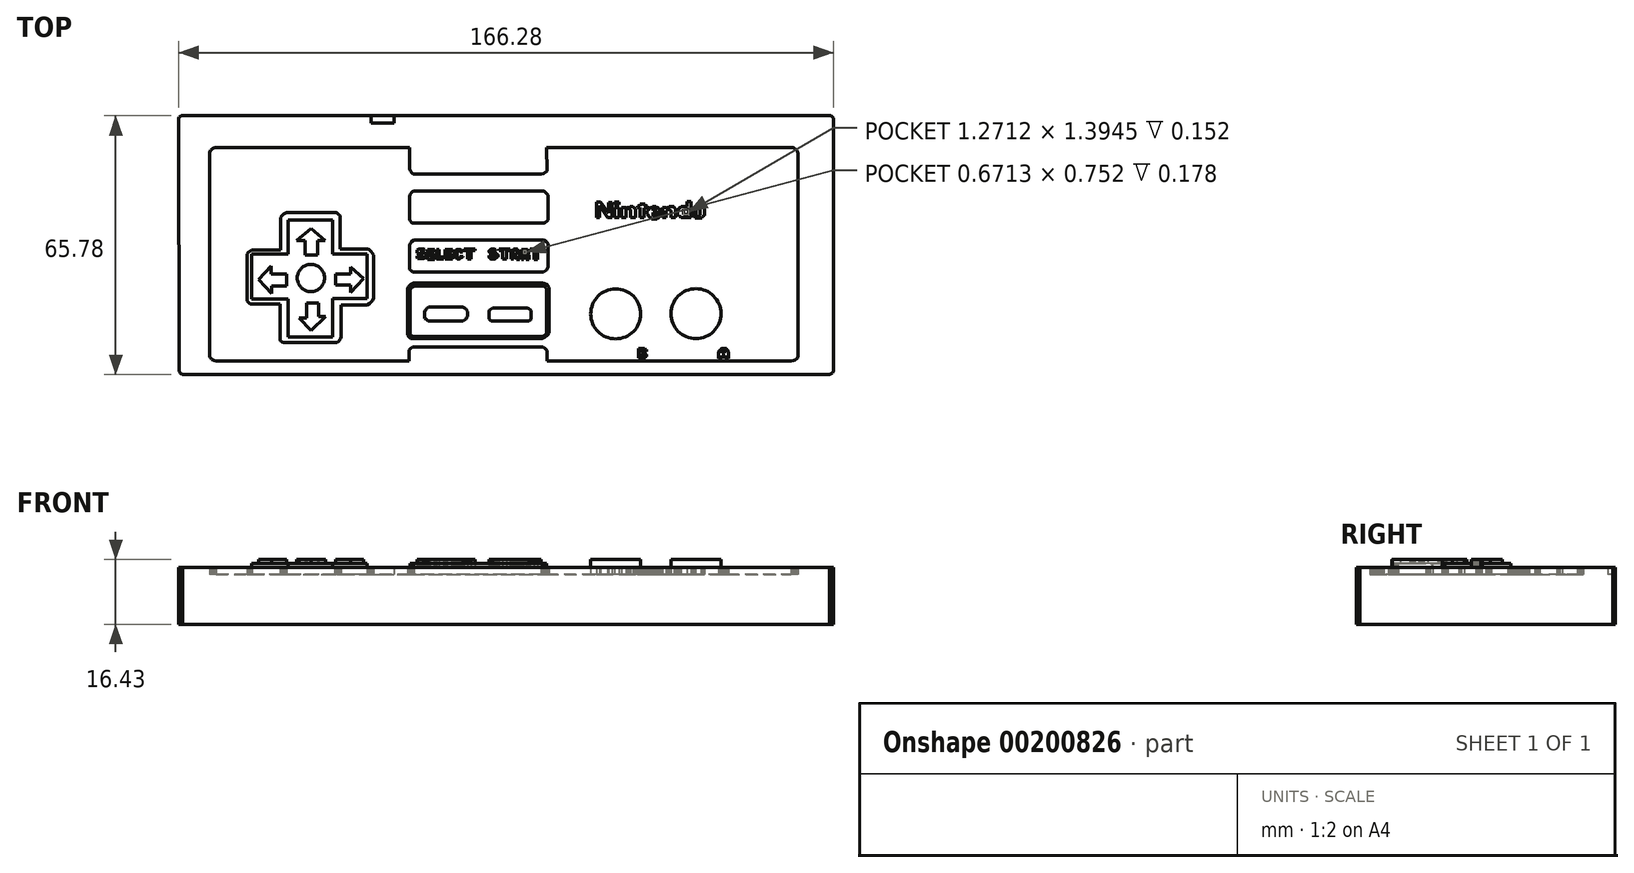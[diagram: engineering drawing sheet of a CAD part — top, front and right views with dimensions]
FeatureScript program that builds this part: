
annotation { "Feature Type Name" : "Feature", "Feature Type Description" : "" }
export const myFeature = defineFeature(function(context is Context, id is Id, definition is map)
    precondition{}
    {
        {
            var Q0;
            Q0=qCreatedBy(makeId("Top.planeOp"),FACE);
            var sketch = newSketch(context, id + "F0", { "sketchPlane" : qUnion([Q0])});
            skLineSegment(sketch, "E0", {"start": v(-67.86, 49.1) * mm, "end": v(97.18, 49.1) * mm});
            skLineSegment(sketch, "E1", {"start": v(97.81, 48.49) * mm, "end": v(97.81, -15.77) * mm});
            skLineSegment(sketch, "E2", {"start": v(96.88, -16.7) * mm, "end": v(-67.5, -16.7) * mm});
            skLineSegment(sketch, "E3", {"start": v(-68.37, -15.86) * mm, "end": v(-68.47, 48.53) * mm});
            skLineSegment(sketch, "E4", {"start": v(-59.29, 40.98) * mm, "end": v(87.55, 40.98) * mm});
            skLineSegment(sketch, "E5", {"start": v(87.1, -13.25) * mm, "end": v(-59.07, -13.25) * mm});
            skLineSegment(sketch, "E6", {"start": v(-60.62, -12.14) * mm, "end": v(-60.7, 39.73) * mm});
            skLineSegment(sketch, "E7", {"start": v(-60.7, 39.73) * mm, "end": v(-60.56, 40.11) * mm});
            skLineSegment(sketch, "E8", {"start": v(-60.56, 40.11) * mm, "end": v(-60.37, 40.33) * mm});
            skLineSegment(sketch, "E9", {"start": v(-60.37, 40.33) * mm, "end": v(-60.1, 40.54) * mm});
            skLineSegment(sketch, "E10", {"start": v(-60.1, 40.54) * mm, "end": v(-59.86, 40.75) * mm});
            skLineSegment(sketch, "E11", {"start": v(-59.86, 40.75) * mm, "end": v(-59.62, 40.87) * mm});
            skLineSegment(sketch, "E12", {"start": v(-59.62, 40.87) * mm, "end": v(-59.29, 40.98) * mm});
            skLineSegment(sketch, "E13", {"start": v(-68.47, 48.53) * mm, "end": v(-68.36, 48.7) * mm});
            skLineSegment(sketch, "E14", {"start": v(-68.36, 48.7) * mm, "end": v(-68.18, 48.87) * mm});
            skLineSegment(sketch, "E15", {"start": v(-68.18, 48.87) * mm, "end": v(-68.01, 48.99) * mm});
            skLineSegment(sketch, "E16", {"start": v(-68.01, 48.99) * mm, "end": v(-67.86, 49.1) * mm});
            skLineSegment(sketch, "E17", {"start": v(-68.37, -15.86) * mm, "end": v(-68.29, -16.07) * mm});
            skLineSegment(sketch, "E18", {"start": v(-68.29, -16.07) * mm, "end": v(-68.14, -16.24) * mm});
            skLineSegment(sketch, "E19", {"start": v(-68.14, -16.24) * mm, "end": v(-67.97, -16.42) * mm});
            skLineSegment(sketch, "E20", {"start": v(-67.97, -16.42) * mm, "end": v(-67.8, -16.53) * mm});
            skLineSegment(sketch, "E21", {"start": v(-67.8, -16.53) * mm, "end": v(-67.64, -16.64) * mm});
            skLineSegment(sketch, "E22", {"start": v(-67.64, -16.64) * mm, "end": v(-67.5, -16.7) * mm});
            skLineSegment(sketch, "E23", {"start": v(96.88, -16.7) * mm, "end": v(97.12, -16.6) * mm});
            skLineSegment(sketch, "E24", {"start": v(97.12, -16.6) * mm, "end": v(97.35, -16.42) * mm});
            skLineSegment(sketch, "E25", {"start": v(97.35, -16.42) * mm, "end": v(97.58, -16.25) * mm});
            skLineSegment(sketch, "E26", {"start": v(97.58, -16.25) * mm, "end": v(97.75, -16.1) * mm});
            skLineSegment(sketch, "E27", {"start": v(97.75, -16.1) * mm, "end": v(97.81, -15.77) * mm});
            skLineSegment(sketch, "E28", {"start": v(97.81, 48.49) * mm, "end": v(97.7, 48.62) * mm});
            skLineSegment(sketch, "E29", {"start": v(97.7, 48.62) * mm, "end": v(97.62, 48.75) * mm});
            skLineSegment(sketch, "E30", {"start": v(97.62, 48.75) * mm, "end": v(97.48, 48.9) * mm});
            skLineSegment(sketch, "E31", {"start": v(97.48, 48.9) * mm, "end": v(97.4, 49) * mm});
            skLineSegment(sketch, "E32", {"start": v(97.4, 49) * mm, "end": v(97.18, 49.1) * mm});
            skLineSegment(sketch, "E33", {"start": v(87.55, 40.98) * mm, "end": v(87.83, 40.9) * mm});
            skLineSegment(sketch, "E34", {"start": v(87.83, 40.9) * mm, "end": v(88.15, 40.66) * mm});
            skLineSegment(sketch, "E35", {"start": v(88.15, 40.66) * mm, "end": v(88.37, 40.45) * mm});
            skLineSegment(sketch, "E36", {"start": v(88.37, 40.45) * mm, "end": v(88.55, 40.26) * mm});
            skLineSegment(sketch, "E37", {"start": v(88.55, 40.26) * mm, "end": v(88.7, 39.95) * mm});
            skLineSegment(sketch, "E38", {"start": v(88.7, 39.95) * mm, "end": v(88.83, 39.45) * mm});
            skLineSegment(sketch, "E39", {"start": v(-60.62, -12.14) * mm, "end": v(-60.52, -12.37) * mm});
            skLineSegment(sketch, "E40", {"start": v(-60.52, -12.37) * mm, "end": v(-60.33, -12.6) * mm});
            skLineSegment(sketch, "E41", {"start": v(-60.33, -12.6) * mm, "end": v(-60.1, -12.81) * mm});
            skLineSegment(sketch, "E42", {"start": v(-60.1, -12.81) * mm, "end": v(-59.8, -12.99) * mm});
            skLineSegment(sketch, "E43", {"start": v(-59.8, -12.99) * mm, "end": v(-59.51, -13.14) * mm});
            skLineSegment(sketch, "E44", {"start": v(-59.51, -13.14) * mm, "end": v(-59.07, -13.25) * mm});
            skLineSegment(sketch, "E45", {"start": v(87.1, -13.25) * mm, "end": v(87.72, -13.15) * mm});
            skLineSegment(sketch, "E46", {"start": v(87.72, -13.15) * mm, "end": v(88.1, -12.98) * mm});
            skLineSegment(sketch, "E47", {"start": v(88.1, -12.98) * mm, "end": v(88.5, -12.67) * mm});
            skLineSegment(sketch, "E48", {"start": v(88.5, -12.67) * mm, "end": v(88.67, -12.46) * mm});
            skLineSegment(sketch, "E49", {"start": v(88.67, -12.46) * mm, "end": v(88.83, -11.98) * mm});
            skCircle(sketch, "E50", {"center": v(42.5, -1.27) * mm, "radius": 6.35 * mm});
            skCircle(sketch, "E51", {"center": v(62.9, -1.22) * mm, "radius": 6.35 * mm});
            skLineSegment(sketch, "E52", {"start": v(48.28, -10.13) * mm, "end": v(48.28, -12.48) * mm});
            skLineSegment(sketch, "E53", {"start": v(48.28, -12.48) * mm, "end": v(49.67, -12.48) * mm});
            skLineSegment(sketch, "E54", {"start": v(49.87, -12.33) * mm, "end": v(50.1, -12.33) * mm});
            skLineSegment(sketch, "E55", {"start": v(50.1, -12.33) * mm, "end": v(50.1, -12.13) * mm});
            skLineSegment(sketch, "E56", {"start": v(50.1, -12.13) * mm, "end": v(50.3, -12.13) * mm});
            skLineSegment(sketch, "E57", {"start": v(50.3, -12.13) * mm, "end": v(50.3, -11.55) * mm});
            skLineSegment(sketch, "E58", {"start": v(50.3, -11.55) * mm, "end": v(50.14, -11.55) * mm});
            skLineSegment(sketch, "E59", {"start": v(50.14, -11.55) * mm, "end": v(50.14, -11.38) * mm});
            skLineSegment(sketch, "E60", {"start": v(50.14, -11.38) * mm, "end": v(49.9, -11.38) * mm});
            skLineSegment(sketch, "E61", {"start": v(49.9, -11.38) * mm, "end": v(49.9, -11.26) * mm});
            skLineSegment(sketch, "E62", {"start": v(49.9, -11.26) * mm, "end": v(49.67, -11.26) * mm});
            skLineSegment(sketch, "E63", {"start": v(49.67, -11.26) * mm, "end": v(49.67, -11.02) * mm});
            skLineSegment(sketch, "E64", {"start": v(49.67, -11.02) * mm, "end": v(49.85, -11.02) * mm});
            skLineSegment(sketch, "E65", {"start": v(49.85, -11.02) * mm, "end": v(49.85, -10.82) * mm});
            skLineSegment(sketch, "E66", {"start": v(49.85, -10.82) * mm, "end": v(50.29, -10.82) * mm});
            skLineSegment(sketch, "E67", {"start": v(50.29, -10.82) * mm, "end": v(50.29, -10.28) * mm});
            skLineSegment(sketch, "E68", {"start": v(50.29, -10.28) * mm, "end": v(49.87, -10.28) * mm});
            skLineSegment(sketch, "E69", {"start": v(49.87, -10.28) * mm, "end": v(49.87, -10.05) * mm});
            skLineSegment(sketch, "E70", {"start": v(49.87, -10.05) * mm, "end": v(48.28, -10.05) * mm});
            skLineSegment(sketch, "E71", {"start": v(48.28, -10.05) * mm, "end": v(48.28, -10.13) * mm});
            skLineSegment(sketch, "E72", {"start": v(49.67, -12.48) * mm, "end": v(49.67, -12.33) * mm});
            skLineSegment(sketch, "E73", {"start": v(49.67, -12.33) * mm, "end": v(49.87, -12.33) * mm});
            skLineSegment(sketch, "E74", {"start": v(49.01, -10.2) * mm, "end": v(49.38, -10.2) * mm});
            skLineSegment(sketch, "E75", {"start": v(49.38, -10.2) * mm, "end": v(49.51, -10.33) * mm});
            skLineSegment(sketch, "E76", {"start": v(48.9, -10.3) * mm, "end": v(49.01, -10.2) * mm});
            skLineSegment(sketch, "E77", {"start": v(49.51, -10.33) * mm, "end": v(49.51, -10.82) * mm});
            skLineSegment(sketch, "E78", {"start": v(49.51, -10.82) * mm, "end": v(49.4, -10.98) * mm});
            skLineSegment(sketch, "E79", {"start": v(49.4, -10.98) * mm, "end": v(49.02, -10.98) * mm});
            skLineSegment(sketch, "E80", {"start": v(49.02, -10.98) * mm, "end": v(48.9, -10.82) * mm});
            skLineSegment(sketch, "E81", {"start": v(48.9, -10.82) * mm, "end": v(48.9, -10.3) * mm});
            skLineSegment(sketch, "E82", {"start": v(49.02, -11.4) * mm, "end": v(49.33, -11.4) * mm});
            skLineSegment(sketch, "E83", {"start": v(49.33, -11.4) * mm, "end": v(49.45, -11.55) * mm});
            skLineSegment(sketch, "E84", {"start": v(49.45, -11.55) * mm, "end": v(49.45, -12.1) * mm});
            skLineSegment(sketch, "E85", {"start": v(49.45, -12.1) * mm, "end": v(49.33, -12.2) * mm});
            skLineSegment(sketch, "E86", {"start": v(49.33, -12.2) * mm, "end": v(49.01, -12.2) * mm});
            skLineSegment(sketch, "E87", {"start": v(49.01, -12.2) * mm, "end": v(48.91, -12.1) * mm});
            skLineSegment(sketch, "E88", {"start": v(48.91, -12.1) * mm, "end": v(48.91, -11.55) * mm});
            skLineSegment(sketch, "E89", {"start": v(48.91, -11.55) * mm, "end": v(49.02, -11.4) * mm});
            skLineSegment(sketch, "E90", {"start": v(68.62, -12.62) * mm, "end": v(69.49, -12.62) * mm});
            skLineSegment(sketch, "E91", {"start": v(69.49, -12.62) * mm, "end": v(69.49, -11.82) * mm});
            skLineSegment(sketch, "E92", {"start": v(69.49, -11.82) * mm, "end": v(70.26, -11.82) * mm});
            skLineSegment(sketch, "E93", {"start": v(70.26, -11.82) * mm, "end": v(70.26, -12.62) * mm});
            skLineSegment(sketch, "E94", {"start": v(70.26, -12.62) * mm, "end": v(71.22, -12.62) * mm});
            skLineSegment(sketch, "E95", {"start": v(71.22, -12.62) * mm, "end": v(71.22, -10.98) * mm});
            skLineSegment(sketch, "E96", {"start": v(71.22, -10.98) * mm, "end": v(71.09, -10.98) * mm});
            skLineSegment(sketch, "E97", {"start": v(71.09, -10.98) * mm, "end": v(71.09, -10.61) * mm});
            skLineSegment(sketch, "E98", {"start": v(71.09, -10.61) * mm, "end": v(70.87, -10.61) * mm});
            skLineSegment(sketch, "E99", {"start": v(70.87, -10.61) * mm, "end": v(70.87, -10.27) * mm});
            skLineSegment(sketch, "E100", {"start": v(70.87, -10.27) * mm, "end": v(70.7, -10.27) * mm});
            skLineSegment(sketch, "E101", {"start": v(70.7, -10.27) * mm, "end": v(70.7, -10.06) * mm});
            skLineSegment(sketch, "E102", {"start": v(70.7, -10.06) * mm, "end": v(69.34, -10.06) * mm});
            skLineSegment(sketch, "E103", {"start": v(69.34, -10.06) * mm, "end": v(69.34, -10.16) * mm});
            skLineSegment(sketch, "E104", {"start": v(69.34, -10.16) * mm, "end": v(69.15, -10.16) * mm});
            skLineSegment(sketch, "E105", {"start": v(69.15, -10.16) * mm, "end": v(69.15, -10.3) * mm});
            skLineSegment(sketch, "E106", {"start": v(69.15, -10.3) * mm, "end": v(68.98, -10.3) * mm});
            skLineSegment(sketch, "E107", {"start": v(68.98, -10.3) * mm, "end": v(68.98, -10.53) * mm});
            skLineSegment(sketch, "E108", {"start": v(68.98, -10.53) * mm, "end": v(68.76, -10.53) * mm});
            skLineSegment(sketch, "E109", {"start": v(68.76, -10.53) * mm, "end": v(68.76, -10.98) * mm});
            skPoint(sketch, "E109.endSnap0", {"position": v(71.15, -10.98) * mm});
            skLineSegment(sketch, "E110", {"start": v(68.76, -10.98) * mm, "end": v(68.62, -10.98) * mm});
            skLineSegment(sketch, "E111", {"start": v(68.62, -10.98) * mm, "end": v(68.62, -12.62) * mm});
            skLineSegment(sketch, "E112", {"start": v(69.54, -11.2) * mm, "end": v(70.2, -11.2) * mm});
            skLineSegment(sketch, "E113", {"start": v(70.2, -11.2) * mm, "end": v(70.2, -10.57) * mm});
            skLineSegment(sketch, "E114", {"start": v(70.2, -10.57) * mm, "end": v(70.05, -10.57) * mm});
            skLineSegment(sketch, "E115", {"start": v(70.05, -10.57) * mm, "end": v(70.05, -10.32) * mm});
            skLineSegment(sketch, "E116", {"start": v(70.05, -10.32) * mm, "end": v(69.76, -10.32) * mm});
            skLineSegment(sketch, "E117", {"start": v(69.76, -10.32) * mm, "end": v(69.76, -10.57) * mm});
            skLineSegment(sketch, "E118", {"start": v(69.76, -10.57) * mm, "end": v(69.54, -10.57) * mm});
            skLineSegment(sketch, "E119", {"start": v(69.54, -10.57) * mm, "end": v(69.54, -11.2) * mm});
            skCircle(sketch, "E120", {"center": v(-34.93, 7.86) * mm, "radius": 3.45 * mm});
            skLineSegment(sketch, "E121", {"start": v(-6, 14.79) * mm, "end": v(-6, 15.14) * mm});
            skLineSegment(sketch, "E122", {"start": v(-6, 15.14) * mm, "end": v(-6.3, 15.25) * mm});
            skLineSegment(sketch, "E123", {"start": v(-6.3, 15.25) * mm, "end": v(-6.6, 15.25) * mm});
            skLineSegment(sketch, "E124", {"start": v(-6.6, 15.25) * mm, "end": v(-7.12, 15.25) * mm});
            skLineSegment(sketch, "E125", {"start": v(-7.12, 15.25) * mm, "end": v(-7.4, 15.25) * mm});
            skLineSegment(sketch, "E126", {"start": v(-7.4, 15.25) * mm, "end": v(-7.74, 15.12) * mm});
            skLineSegment(sketch, "E127", {"start": v(-7.74, 15.12) * mm, "end": v(-7.9, 14.94) * mm});
            skLineSegment(sketch, "E128", {"start": v(-7.9, 14.94) * mm, "end": v(-7.9, 14.53) * mm});
            skLineSegment(sketch, "E129", {"start": v(-7.9, 14.53) * mm, "end": v(-7.9, 14.2) * mm});
            skLineSegment(sketch, "E130", {"start": v(-7.9, 14.2) * mm, "end": v(-7.72, 14.03) * mm});
            skLineSegment(sketch, "E131", {"start": v(-7.72, 14.03) * mm, "end": v(-7.44, 13.9) * mm});
            skLineSegment(sketch, "E132", {"start": v(-7.44, 13.9) * mm, "end": v(-7.07, 13.9) * mm});
            skLineSegment(sketch, "E133", {"start": v(-7.07, 13.9) * mm, "end": v(-6.62, 13.75) * mm});
            skLineSegment(sketch, "E134", {"start": v(-6.62, 13.75) * mm, "end": v(-6.45, 13.57) * mm});
            skLineSegment(sketch, "E135", {"start": v(-6.45, 13.57) * mm, "end": v(-6.45, 13.37) * mm});
            skLineSegment(sketch, "E136", {"start": v(-6.45, 13.37) * mm, "end": v(-6.6, 13.27) * mm});
            skLineSegment(sketch, "E137", {"start": v(-6.6, 13.27) * mm, "end": v(-7.28, 13.27) * mm});
            skLineSegment(sketch, "E138", {"start": v(-7.28, 13.27) * mm, "end": v(-7.55, 13.44) * mm});
            skLineSegment(sketch, "E139", {"start": v(-7.55, 13.44) * mm, "end": v(-7.9, 13.44) * mm});
            skLineSegment(sketch, "E140", {"start": v(-7.9, 13.44) * mm, "end": v(-7.9, 13.15) * mm});
            skLineSegment(sketch, "E141", {"start": v(-7.9, 13.15) * mm, "end": v(-7.76, 12.81) * mm});
            skLineSegment(sketch, "E142", {"start": v(-7.76, 12.81) * mm, "end": v(-7.37, 12.81) * mm});
            skLineSegment(sketch, "E143", {"start": v(-7.37, 12.81) * mm, "end": v(-6.74, 12.81) * mm});
            skLineSegment(sketch, "E144", {"start": v(-6.74, 12.81) * mm, "end": v(-6.24, 12.81) * mm});
            skLineSegment(sketch, "E145", {"start": v(-6.24, 12.81) * mm, "end": v(-5.81, 13.02) * mm});
            skLineSegment(sketch, "E146", {"start": v(-5.81, 13.02) * mm, "end": v(-5.67, 13.3) * mm});
            skLineSegment(sketch, "E147", {"start": v(-5.67, 13.3) * mm, "end": v(-5.57, 13.57) * mm});
            skLineSegment(sketch, "E148", {"start": v(-5.57, 13.57) * mm, "end": v(-5.68, 13.84) * mm});
            skLineSegment(sketch, "E149", {"start": v(-5.68, 13.84) * mm, "end": v(-5.93, 14.06) * mm});
            skLineSegment(sketch, "E150", {"start": v(-5.93, 14.06) * mm, "end": v(-6.23, 14.24) * mm});
            skLineSegment(sketch, "E151", {"start": v(-6.23, 14.24) * mm, "end": v(-6.76, 14.24) * mm});
            skLineSegment(sketch, "E152", {"start": v(-6.76, 14.24) * mm, "end": v(-7.05, 14.37) * mm});
            skLineSegment(sketch, "E153", {"start": v(-7.05, 14.37) * mm, "end": v(-7.16, 14.55) * mm});
            skLineSegment(sketch, "E154", {"start": v(-7.16, 14.55) * mm, "end": v(-6.99, 14.67) * mm});
            skLineSegment(sketch, "E155", {"start": v(-6.99, 14.67) * mm, "end": v(-6.7, 14.67) * mm});
            skLineSegment(sketch, "E156", {"start": v(-6.7, 14.67) * mm, "end": v(-6.24, 14.67) * mm});
            skLineSegment(sketch, "E157", {"start": v(-6.24, 14.67) * mm, "end": v(-6, 14.79) * mm});
            skLineSegment(sketch, "E158", {"start": v(-3.45, 15.14) * mm, "end": v(-3.45, 14.79) * mm});
            skLineSegment(sketch, "E159", {"start": v(-3.45, 14.79) * mm, "end": v(-4.75, 14.79) * mm});
            skLineSegment(sketch, "E160", {"start": v(-4.75, 14.79) * mm, "end": v(-4.75, 14.07) * mm});
            skLineSegment(sketch, "E161", {"start": v(-4.75, 14.07) * mm, "end": v(-3.68, 14.07) * mm});
            skLineSegment(sketch, "E162", {"start": v(-3.68, 14.07) * mm, "end": v(-3.68, 13.7) * mm});
            skLineSegment(sketch, "E163", {"start": v(-3.68, 13.7) * mm, "end": v(-4.68, 13.7) * mm});
            skLineSegment(sketch, "E164", {"start": v(-4.68, 13.7) * mm, "end": v(-4.68, 13.12) * mm});
            skLineSegment(sketch, "E165", {"start": v(-4.68, 13.12) * mm, "end": v(-3.48, 13.12) * mm});
            skLineSegment(sketch, "E166", {"start": v(-3.48, 13.12) * mm, "end": v(-3.48, 12.6) * mm});
            skLineSegment(sketch, "E167", {"start": v(-3.48, 12.6) * mm, "end": v(-5.3, 12.6) * mm});
            skLineSegment(sketch, "E168", {"start": v(-5.3, 12.6) * mm, "end": v(-5.3, 15.14) * mm});
            skPoint(sketch, "E169.start.orphan", {"position": v(-5.3, 15.14) * mm});
            skLineSegment(sketch, "E170", {"start": v(-3.45, 15.14) * mm, "end": v(-5.3, 15.14) * mm});
            skLineSegment(sketch, "E171", {"start": v(-2.89, 15.14) * mm, "end": v(-2.33, 15.14) * mm});
            skLineSegment(sketch, "E172", {"start": v(-2.33, 15.14) * mm, "end": v(-2.33, 13.12) * mm});
            skLineSegment(sketch, "E173", {"start": v(-2.33, 13.12) * mm, "end": v(-1.24, 13.12) * mm});
            skLineSegment(sketch, "E174", {"start": v(-1.24, 13.12) * mm, "end": v(-1.24, 12.61) * mm});
            skLineSegment(sketch, "E175", {"start": v(-1.24, 12.61) * mm, "end": v(-2.94, 12.61) * mm});
            skLineSegment(sketch, "E176", {"start": v(-2.94, 12.61) * mm, "end": v(-2.94, 15.14) * mm});
            skLineSegment(sketch, "E177", {"start": v(-0.76, 15.14) * mm, "end": v(1.05, 15.14) * mm});
            skLineSegment(sketch, "E178", {"start": v(1.05, 15.14) * mm, "end": v(1.05, 14.76) * mm});
            skLineSegment(sketch, "E179", {"start": v(1.05, 14.76) * mm, "end": v(-0.32, 14.76) * mm});
            skLineSegment(sketch, "E180", {"start": v(-0.32, 14.76) * mm, "end": v(-0.32, 14.07) * mm});
            skLineSegment(sketch, "E181", {"start": v(-0.32, 14.07) * mm, "end": v(0.87, 14.07) * mm});
            skLineSegment(sketch, "E182", {"start": v(0.87, 14.07) * mm, "end": v(0.87, 13.65) * mm});
            skLineSegment(sketch, "E183", {"start": v(0.87, 13.65) * mm, "end": v(-0.32, 13.65) * mm});
            skLineSegment(sketch, "E184", {"start": v(-0.32, 13.65) * mm, "end": v(-0.32, 13.14) * mm});
            skLineSegment(sketch, "E185", {"start": v(-0.32, 13.14) * mm, "end": v(1.09, 13.14) * mm});
            skLineSegment(sketch, "E186", {"start": v(1.09, 13.14) * mm, "end": v(1.09, 12.62) * mm});
            skLineSegment(sketch, "E187", {"start": v(1.09, 12.62) * mm, "end": v(-0.85, 12.62) * mm});
            skLineSegment(sketch, "E188", {"start": v(-0.85, 12.62) * mm, "end": v(-0.85, 15.14) * mm});
            skLineSegment(sketch, "E189", {"start": v(-0.85, 15.14) * mm, "end": v(-0.76, 15.14) * mm});
            skLineSegment(sketch, "E190", {"start": v(2.97, 14.4) * mm, "end": v(3.62, 14.4) * mm});
            skLineSegment(sketch, "E191", {"start": v(3.62, 14.4) * mm, "end": v(3.62, 14.53) * mm});
            skLineSegment(sketch, "E192", {"start": v(3.62, 14.53) * mm, "end": v(3.47, 14.53) * mm});
            skLineSegment(sketch, "E193", {"start": v(3.47, 14.53) * mm, "end": v(3.47, 14.66) * mm});
            skLineSegment(sketch, "E194", {"start": v(3.47, 14.66) * mm, "end": v(3.38, 14.66) * mm});
            skLineSegment(sketch, "E195", {"start": v(3.38, 14.66) * mm, "end": v(3.38, 14.9) * mm});
            skLineSegment(sketch, "E196", {"start": v(3.38, 14.9) * mm, "end": v(3.07, 14.9) * mm});
            skLineSegment(sketch, "E197", {"start": v(3.07, 14.9) * mm, "end": v(3.07, 15.14) * mm});
            skLineSegment(sketch, "E198", {"start": v(3.07, 15.14) * mm, "end": v(2.13, 15.14) * mm});
            skLineSegment(sketch, "E199", {"start": v(2.13, 15.14) * mm, "end": v(2.13, 14.9) * mm});
            skLineSegment(sketch, "E200", {"start": v(2.13, 14.9) * mm, "end": v(1.84, 14.9) * mm});
            skLineSegment(sketch, "E201", {"start": v(1.84, 14.9) * mm, "end": v(1.84, 14.7) * mm});
            skLineSegment(sketch, "E202", {"start": v(1.84, 14.7) * mm, "end": v(1.62, 14.7) * mm});
            skLineSegment(sketch, "E203", {"start": v(1.62, 14.7) * mm, "end": v(1.62, 13.18) * mm});
            skLineSegment(sketch, "E204", {"start": v(1.62, 13.18) * mm, "end": v(1.84, 13.18) * mm});
            skLineSegment(sketch, "E205", {"start": v(1.84, 13.18) * mm, "end": v(1.84, 12.86) * mm});
            skLineSegment(sketch, "E206", {"start": v(1.84, 12.86) * mm, "end": v(2.16, 12.86) * mm});
            skLineSegment(sketch, "E207", {"start": v(2.16, 12.86) * mm, "end": v(2.16, 12.64) * mm});
            skLineSegment(sketch, "E208", {"start": v(2.16, 12.64) * mm, "end": v(2.83, 12.64) * mm});
            skLineSegment(sketch, "E209", {"start": v(2.83, 12.64) * mm, "end": v(2.83, 12.85) * mm});
            skLineSegment(sketch, "E210", {"start": v(2.83, 12.85) * mm, "end": v(3.07, 12.85) * mm});
            skLineSegment(sketch, "E211", {"start": v(3.07, 12.85) * mm, "end": v(3.07, 13.02) * mm});
            skLineSegment(sketch, "E212", {"start": v(3.07, 13.02) * mm, "end": v(3.46, 13.02) * mm});
            skLineSegment(sketch, "E213", {"start": v(3.46, 13.02) * mm, "end": v(3.46, 13.23) * mm});
            skLineSegment(sketch, "E214", {"start": v(3.46, 13.23) * mm, "end": v(3.67, 13.23) * mm});
            skLineSegment(sketch, "E215", {"start": v(3.67, 13.23) * mm, "end": v(3.67, 13.36) * mm});
            skLineSegment(sketch, "E216", {"start": v(3.67, 13.36) * mm, "end": v(2.97, 13.36) * mm});
            skLineSegment(sketch, "E217", {"start": v(2.97, 13.36) * mm, "end": v(2.97, 13.15) * mm});
            skLineSegment(sketch, "E218", {"start": v(2.97, 13.15) * mm, "end": v(2.88, 13.15) * mm});
            skLineSegment(sketch, "E219", {"start": v(2.88, 13.15) * mm, "end": v(2.88, 12.96) * mm});
            skLineSegment(sketch, "E220", {"start": v(2.88, 12.96) * mm, "end": v(2.43, 12.96) * mm});
            skLineSegment(sketch, "E221", {"start": v(2.43, 12.96) * mm, "end": v(2.33, 12.96) * mm});
            skLineSegment(sketch, "E222", {"start": v(2.33, 12.96) * mm, "end": v(2.33, 13.06) * mm});
            skLineSegment(sketch, "E223", {"start": v(2.33, 13.06) * mm, "end": v(2.2, 13.06) * mm});
            skLineSegment(sketch, "E224", {"start": v(2.2, 13.06) * mm, "end": v(2.2, 14.67) * mm});
            skLineSegment(sketch, "E225", {"start": v(2.2, 14.67) * mm, "end": v(2.38, 14.67) * mm});
            skLineSegment(sketch, "E226", {"start": v(2.38, 14.67) * mm, "end": v(2.38, 14.92) * mm});
            skLineSegment(sketch, "E227", {"start": v(2.38, 14.92) * mm, "end": v(2.72, 14.92) * mm});
            skLineSegment(sketch, "E228", {"start": v(2.72, 14.92) * mm, "end": v(2.72, 14.69) * mm});
            skLineSegment(sketch, "E229", {"start": v(2.72, 14.69) * mm, "end": v(2.97, 14.69) * mm});
            skLineSegment(sketch, "E230", {"start": v(2.97, 14.69) * mm, "end": v(2.97, 14.4) * mm});
            skLineSegment(sketch, "E231", {"start": v(4.91, 12.64) * mm, "end": v(5.72, 12.64) * mm});
            skLineSegment(sketch, "E232", {"start": v(5.72, 12.64) * mm, "end": v(5.72, 14.87) * mm});
            skLineSegment(sketch, "E233", {"start": v(5.72, 14.87) * mm, "end": v(6.8, 14.87) * mm});
            skLineSegment(sketch, "E234", {"start": v(6.8, 14.87) * mm, "end": v(6.8, 15.23) * mm});
            skLineSegment(sketch, "E235", {"start": v(6.8, 15.23) * mm, "end": v(3.93, 15.23) * mm});
            skLineSegment(sketch, "E236", {"start": v(3.93, 15.23) * mm, "end": v(3.93, 14.87) * mm});
            skLineSegment(sketch, "E237", {"start": v(3.93, 14.87) * mm, "end": v(4.91, 14.87) * mm});
            skLineSegment(sketch, "E238", {"start": v(4.91, 14.87) * mm, "end": v(4.91, 12.64) * mm});
            skLineSegment(sketch, "E239", {"start": v(12.17, 14.77) * mm, "end": v(12.17, 15.1) * mm});
            skLineSegment(sketch, "E240", {"start": v(12.17, 15.1) * mm, "end": v(11.77, 15.1) * mm});
            skLineSegment(sketch, "E241", {"start": v(11.77, 15.1) * mm, "end": v(11.77, 15.25) * mm});
            skLineSegment(sketch, "E242", {"start": v(11.77, 15.25) * mm, "end": v(10.88, 15.25) * mm});
            skLineSegment(sketch, "E243", {"start": v(10.88, 15.25) * mm, "end": v(10.88, 15.12) * mm});
            skLineSegment(sketch, "E244", {"start": v(10.88, 15.12) * mm, "end": v(10.54, 15.12) * mm});
            skLineSegment(sketch, "E245", {"start": v(10.54, 15.12) * mm, "end": v(10.54, 14.99) * mm});
            skLineSegment(sketch, "E246", {"start": v(10.54, 14.99) * mm, "end": v(10.44, 14.99) * mm});
            skLineSegment(sketch, "E247", {"start": v(10.44, 14.99) * mm, "end": v(10.44, 14.87) * mm});
            skLineSegment(sketch, "E248", {"start": v(10.44, 14.87) * mm, "end": v(10.31, 14.87) * mm});
            skLineSegment(sketch, "E249", {"start": v(10.31, 14.87) * mm, "end": v(10.31, 14.4) * mm});
            skLineSegment(sketch, "E250", {"start": v(10.31, 14.4) * mm, "end": v(10.42, 14.4) * mm});
            skLineSegment(sketch, "E251", {"start": v(10.42, 14.4) * mm, "end": v(10.42, 14.21) * mm});
            skLineSegment(sketch, "E252", {"start": v(10.42, 14.21) * mm, "end": v(10.7, 14.21) * mm});
            skLineSegment(sketch, "E253", {"start": v(10.7, 14.21) * mm, "end": v(10.7, 13.94) * mm});
            skLineSegment(sketch, "E254", {"start": v(10.7, 13.94) * mm, "end": v(11.36, 13.94) * mm});
            skLineSegment(sketch, "E255", {"start": v(11.36, 13.94) * mm, "end": v(11.36, 13.7) * mm});
            skLineSegment(sketch, "E256", {"start": v(11.36, 13.7) * mm, "end": v(11.82, 13.7) * mm});
            skLineSegment(sketch, "E257", {"start": v(11.82, 13.7) * mm, "end": v(11.82, 13.58) * mm});
            skLineSegment(sketch, "E258", {"start": v(11.82, 13.58) * mm, "end": v(11.98, 13.58) * mm});
            skLineSegment(sketch, "E259", {"start": v(11.98, 13.58) * mm, "end": v(11.98, 13.39) * mm});
            skLineSegment(sketch, "E260", {"start": v(11.98, 13.39) * mm, "end": v(11.83, 13.39) * mm});
            skLineSegment(sketch, "E261", {"start": v(11.83, 13.39) * mm, "end": v(11.83, 13.23) * mm});
            skLineSegment(sketch, "E262", {"start": v(11.83, 13.23) * mm, "end": v(11.65, 13.23) * mm});
            skLineSegment(sketch, "E263", {"start": v(11.65, 13.23) * mm, "end": v(11.65, 13.11) * mm});
            skLineSegment(sketch, "E264", {"start": v(11.65, 13.11) * mm, "end": v(11.3, 13.11) * mm});
            skLineSegment(sketch, "E265", {"start": v(11.3, 13.11) * mm, "end": v(11.3, 13.23) * mm});
            skLineSegment(sketch, "E266", {"start": v(11.3, 13.23) * mm, "end": v(10.8, 13.23) * mm});
            skLineSegment(sketch, "E267", {"start": v(10.8, 13.23) * mm, "end": v(10.8, 13.41) * mm});
            skLineSegment(sketch, "E268", {"start": v(10.8, 13.41) * mm, "end": v(10.52, 13.41) * mm});
            skLineSegment(sketch, "E269", {"start": v(10.52, 13.41) * mm, "end": v(10.52, 13.54) * mm});
            skLineSegment(sketch, "E270", {"start": v(10.52, 13.54) * mm, "end": v(10.31, 13.54) * mm});
            skLineSegment(sketch, "E271", {"start": v(10.31, 13.54) * mm, "end": v(10.31, 13.04) * mm});
            skLineSegment(sketch, "E272", {"start": v(10.31, 13.04) * mm, "end": v(10.49, 13.04) * mm});
            skLineSegment(sketch, "E273", {"start": v(10.49, 13.04) * mm, "end": v(10.49, 12.82) * mm});
            skLineSegment(sketch, "E274", {"start": v(10.49, 12.82) * mm, "end": v(10.75, 12.82) * mm});
            skLineSegment(sketch, "E275", {"start": v(10.75, 12.82) * mm, "end": v(10.75, 12.7) * mm});
            skLineSegment(sketch, "E276", {"start": v(10.75, 12.7) * mm, "end": v(11.83, 12.7) * mm});
            skLineSegment(sketch, "E277", {"start": v(11.83, 12.7) * mm, "end": v(11.83, 12.84) * mm});
            skLineSegment(sketch, "E278", {"start": v(11.83, 12.84) * mm, "end": v(12.15, 12.84) * mm});
            skLineSegment(sketch, "E279", {"start": v(12.15, 12.84) * mm, "end": v(12.15, 13.02) * mm});
            skLineSegment(sketch, "E280", {"start": v(12.15, 13.02) * mm, "end": v(12.41, 13.02) * mm});
            skLineSegment(sketch, "E281", {"start": v(12.41, 13.02) * mm, "end": v(12.41, 13.15) * mm});
            skLineSegment(sketch, "E282", {"start": v(12.41, 13.15) * mm, "end": v(12.6, 13.15) * mm});
            skLineSegment(sketch, "E283", {"start": v(12.6, 13.15) * mm, "end": v(12.6, 13.87) * mm});
            skLineSegment(sketch, "E284", {"start": v(12.6, 13.87) * mm, "end": v(12.43, 13.87) * mm});
            skLineSegment(sketch, "E285", {"start": v(12.43, 13.87) * mm, "end": v(12.43, 14.04) * mm});
            skLineSegment(sketch, "E286", {"start": v(12.43, 14.04) * mm, "end": v(12.24, 14.04) * mm});
            skLineSegment(sketch, "E287", {"start": v(12.24, 14.04) * mm, "end": v(12.24, 14.23) * mm});
            skLineSegment(sketch, "E288", {"start": v(12.24, 14.23) * mm, "end": v(11.11, 14.23) * mm});
            skLineSegment(sketch, "E289", {"start": v(11.11, 14.23) * mm, "end": v(11.11, 14.4) * mm});
            skLineSegment(sketch, "E290", {"start": v(11.11, 14.4) * mm, "end": v(10.93, 14.4) * mm});
            skLineSegment(sketch, "E291", {"start": v(10.93, 14.4) * mm, "end": v(10.93, 14.69) * mm});
            skLineSegment(sketch, "E292", {"start": v(10.93, 14.69) * mm, "end": v(11.07, 14.69) * mm});
            skLineSegment(sketch, "E293", {"start": v(11.07, 14.69) * mm, "end": v(11.07, 14.87) * mm});
            skLineSegment(sketch, "E294", {"start": v(11.07, 14.87) * mm, "end": v(11.5, 14.87) * mm});
            skLineSegment(sketch, "E295", {"start": v(11.5, 14.87) * mm, "end": v(11.5, 14.77) * mm});
            skLineSegment(sketch, "E296", {"start": v(11.5, 14.77) * mm, "end": v(12.17, 14.77) * mm});
            skLineSegment(sketch, "E297", {"start": v(13.78, 12.64) * mm, "end": v(14.76, 12.64) * mm});
            skLineSegment(sketch, "E298", {"start": v(14.76, 12.64) * mm, "end": v(14.76, 14.87) * mm});
            skLineSegment(sketch, "E299", {"start": v(14.76, 14.87) * mm, "end": v(15.68, 14.87) * mm});
            skLineSegment(sketch, "E300", {"start": v(15.68, 14.87) * mm, "end": v(15.68, 15.22) * mm});
            skLineSegment(sketch, "E301", {"start": v(15.68, 15.22) * mm, "end": v(12.88, 15.22) * mm});
            skLineSegment(sketch, "E302", {"start": v(12.88, 15.22) * mm, "end": v(12.88, 14.87) * mm});
            skLineSegment(sketch, "E303", {"start": v(12.88, 14.87) * mm, "end": v(13.78, 14.87) * mm});
            skLineSegment(sketch, "E304", {"start": v(13.78, 14.87) * mm, "end": v(13.78, 12.64) * mm});
            skLineSegment(sketch, "E305", {"start": v(16.53, 12.64) * mm, "end": v(16.53, 13.45) * mm});
            skLineSegment(sketch, "E306", {"start": v(16.53, 13.45) * mm, "end": v(16.83, 13.45) * mm});
            skLineSegment(sketch, "E307", {"start": v(16.83, 13.45) * mm, "end": v(16.83, 13.62) * mm});
            skLineSegment(sketch, "E308", {"start": v(16.83, 13.62) * mm, "end": v(17.02, 13.62) * mm});
            skLineSegment(sketch, "E309", {"start": v(17.02, 13.62) * mm, "end": v(17.02, 13.42) * mm});
            skLineSegment(sketch, "E310", {"start": v(17.02, 13.42) * mm, "end": v(17.38, 13.42) * mm});
            skLineSegment(sketch, "E311", {"start": v(17.38, 13.42) * mm, "end": v(17.38, 12.57) * mm});
            skLineSegment(sketch, "E312", {"start": v(18.08, 13.66) * mm, "end": v(18.08, 14.55) * mm});
            skLineSegment(sketch, "E313", {"start": v(18.08, 14.55) * mm, "end": v(17.86, 14.55) * mm});
            skLineSegment(sketch, "E314", {"start": v(17.86, 14.55) * mm, "end": v(17.86, 14.87) * mm});
            skLineSegment(sketch, "E315", {"start": v(17.86, 14.87) * mm, "end": v(17.69, 14.87) * mm});
            skLineSegment(sketch, "E316", {"start": v(17.69, 14.87) * mm, "end": v(17.69, 15) * mm});
            skLineSegment(sketch, "E317", {"start": v(17.69, 15) * mm, "end": v(17.51, 15) * mm});
            skLineSegment(sketch, "E318", {"start": v(17.51, 15) * mm, "end": v(17.51, 15.18) * mm});
            skLineSegment(sketch, "E319", {"start": v(17.51, 15.18) * mm, "end": v(16.58, 15.18) * mm});
            skLineSegment(sketch, "E320", {"start": v(16.58, 15.18) * mm, "end": v(16.58, 15) * mm});
            skLineSegment(sketch, "E321", {"start": v(16.58, 15) * mm, "end": v(16.36, 15) * mm});
            skLineSegment(sketch, "E322", {"start": v(16.36, 15) * mm, "end": v(16.36, 14.87) * mm});
            skLineSegment(sketch, "E323", {"start": v(16.36, 14.87) * mm, "end": v(16.14, 14.87) * mm});
            skLineSegment(sketch, "E324", {"start": v(16.14, 14.87) * mm, "end": v(16.14, 14.55) * mm});
            skLineSegment(sketch, "E325", {"start": v(16.14, 14.55) * mm, "end": v(15.96, 14.55) * mm});
            skLineSegment(sketch, "E326", {"start": v(15.96, 14.55) * mm, "end": v(15.96, 13.7) * mm});
            skLineSegment(sketch, "E327", {"start": v(17.38, 12.57) * mm, "end": v(18.08, 12.57) * mm});
            skLineSegment(sketch, "E328", {"start": v(18.08, 12.57) * mm, "end": v(18.08, 13.66) * mm});
            skLineSegment(sketch, "E329", {"start": v(16.53, 12.64) * mm, "end": v(15.96, 12.64) * mm});
            skLineSegment(sketch, "E330", {"start": v(15.96, 12.64) * mm, "end": v(15.96, 13.7) * mm});
            skLineSegment(sketch, "E331", {"start": v(18.58, 15.07) * mm, "end": v(18.58, 12.57) * mm});
            skLineSegment(sketch, "E332", {"start": v(18.58, 12.57) * mm, "end": v(19.1, 12.57) * mm});
            skLineSegment(sketch, "E333", {"start": v(19.1, 12.57) * mm, "end": v(19.1, 13.57) * mm});
            skLineSegment(sketch, "E334", {"start": v(19.1, 13.57) * mm, "end": v(19.76, 13.57) * mm});
            skLineSegment(sketch, "E335", {"start": v(19.76, 13.57) * mm, "end": v(19.76, 12.57) * mm});
            skLineSegment(sketch, "E336", {"start": v(19.76, 12.57) * mm, "end": v(20.52, 12.57) * mm});
            skLineSegment(sketch, "E337", {"start": v(20.52, 12.57) * mm, "end": v(20.52, 13.64) * mm});
            skLineSegment(sketch, "E338", {"start": v(20.52, 13.64) * mm, "end": v(20.2, 13.64) * mm});
            skLineSegment(sketch, "E339", {"start": v(20.2, 13.64) * mm, "end": v(20.2, 13.97) * mm});
            skLineSegment(sketch, "E340", {"start": v(20.2, 13.97) * mm, "end": v(20.4, 13.97) * mm});
            skLineSegment(sketch, "E341", {"start": v(20.4, 13.97) * mm, "end": v(20.4, 14.89) * mm});
            skLineSegment(sketch, "E342", {"start": v(20.4, 14.89) * mm, "end": v(20.08, 14.89) * mm});
            skLineSegment(sketch, "E343", {"start": v(20.08, 14.89) * mm, "end": v(20.08, 15.07) * mm});
            skLineSegment(sketch, "E344", {"start": v(20.08, 15.07) * mm, "end": v(18.58, 15.07) * mm});
            skLineSegment(sketch, "E345", {"start": v(16.8, 15) * mm, "end": v(17.12, 15) * mm});
            skLineSegment(sketch, "E346", {"start": v(17.12, 15) * mm, "end": v(17.12, 14.81) * mm});
            skLineSegment(sketch, "E347", {"start": v(17.12, 14.81) * mm, "end": v(17.3, 14.81) * mm});
            skLineSegment(sketch, "E348", {"start": v(17.3, 14.81) * mm, "end": v(17.3, 14.63) * mm});
            skLineSegment(sketch, "E349", {"start": v(17.3, 14.63) * mm, "end": v(17.46, 14.63) * mm});
            skLineSegment(sketch, "E350", {"start": v(17.46, 14.63) * mm, "end": v(17.46, 13.87) * mm});
            skLineSegment(sketch, "E351", {"start": v(17.46, 13.87) * mm, "end": v(16.47, 13.87) * mm});
            skLineSegment(sketch, "E352", {"start": v(16.47, 13.87) * mm, "end": v(16.47, 14.63) * mm});
            skLineSegment(sketch, "E353", {"start": v(16.47, 14.63) * mm, "end": v(16.63, 14.63) * mm});
            skLineSegment(sketch, "E354", {"start": v(16.63, 14.63) * mm, "end": v(16.63, 14.81) * mm});
            skLineSegment(sketch, "E355", {"start": v(16.63, 14.81) * mm, "end": v(16.8, 14.81) * mm});
            skLineSegment(sketch, "E356", {"start": v(16.8, 14.81) * mm, "end": v(16.8, 15) * mm});
            skLineSegment(sketch, "E357", {"start": v(19.1, 14.06) * mm, "end": v(19.78, 14.06) * mm});
            skLineSegment(sketch, "E358", {"start": v(19.78, 14.06) * mm, "end": v(19.78, 14.81) * mm});
            skLineSegment(sketch, "E359", {"start": v(19.78, 14.81) * mm, "end": v(19.1, 14.81) * mm});
            skLineSegment(sketch, "E360", {"start": v(19.1, 14.81) * mm, "end": v(19.1, 14.06) * mm});
            skLineSegment(sketch, "E361", {"start": v(21.8, 12.57) * mm, "end": v(22.62, 12.57) * mm});
            skLineSegment(sketch, "E362", {"start": v(22.62, 12.57) * mm, "end": v(22.62, 14.89) * mm});
            skLineSegment(sketch, "E363", {"start": v(22.62, 14.89) * mm, "end": v(23.56, 14.89) * mm});
            skLineSegment(sketch, "E364", {"start": v(23.56, 14.89) * mm, "end": v(23.56, 15.22) * mm});
            skLineSegment(sketch, "E365", {"start": v(23.56, 15.22) * mm, "end": v(20.8, 15.22) * mm});
            skLineSegment(sketch, "E366", {"start": v(20.8, 15.22) * mm, "end": v(20.8, 14.89) * mm});
            skLineSegment(sketch, "E367", {"start": v(20.8, 14.89) * mm, "end": v(21.8, 14.89) * mm});
            skLineSegment(sketch, "E368", {"start": v(21.8, 14.89) * mm, "end": v(21.8, 12.57) * mm});
            skLineSegment(sketch, "E369", {"start": v(37.69, 23.27) * mm, "end": v(38.4, 23.27) * mm});
            skLineSegment(sketch, "E370", {"start": v(38.4, 23.27) * mm, "end": v(38.4, 26.27) * mm});
            skLineSegment(sketch, "E371", {"start": v(38.4, 26.27) * mm, "end": v(40.5, 23.25) * mm});
            skLineSegment(sketch, "E372", {"start": v(40.5, 23.25) * mm, "end": v(41.64, 23.25) * mm});
            skLineSegment(sketch, "E373", {"start": v(41.64, 23.25) * mm, "end": v(41.64, 27.08) * mm});
            skLineSegment(sketch, "E374", {"start": v(41.64, 27.08) * mm, "end": v(40.64, 27.08) * mm});
            skLineSegment(sketch, "E375", {"start": v(40.64, 27.08) * mm, "end": v(40.64, 24.3) * mm});
            skLineSegment(sketch, "E376", {"start": v(40.64, 24.3) * mm, "end": v(38.62, 27.12) * mm});
            skLineSegment(sketch, "E377", {"start": v(38.62, 27.12) * mm, "end": v(37.69, 27.12) * mm});
            skLineSegment(sketch, "E378", {"start": v(37.69, 27.12) * mm, "end": v(37.69, 23.27) * mm});
            skLineSegment(sketch, "E379", {"start": v(42.24, 23.25) * mm, "end": v(43.36, 23.25) * mm});
            skLineSegment(sketch, "E380", {"start": v(43.36, 23.25) * mm, "end": v(43.36, 25.73) * mm});
            skLineSegment(sketch, "E381", {"start": v(43.36, 25.73) * mm, "end": v(42.24, 25.73) * mm});
            skLineSegment(sketch, "E382", {"start": v(42.24, 25.73) * mm, "end": v(42.24, 23.25) * mm});
            skLineSegment(sketch, "E383", {"start": v(42.24, 26.55) * mm, "end": v(43.37, 26.55) * mm});
            skLineSegment(sketch, "E384", {"start": v(43.37, 26.55) * mm, "end": v(43.37, 27.12) * mm});
            skLineSegment(sketch, "E385", {"start": v(43.37, 27.12) * mm, "end": v(42.24, 27.12) * mm});
            skLineSegment(sketch, "E386", {"start": v(42.24, 27.12) * mm, "end": v(42.24, 26.55) * mm});
            skLineSegment(sketch, "E387", {"start": v(43.97, 23.25) * mm, "end": v(45.16, 23.25) * mm});
            skLineSegment(sketch, "E388", {"start": v(45.16, 23.25) * mm, "end": v(45.16, 25.3) * mm});
            skLineSegment(sketch, "E389", {"start": v(45.16, 25.3) * mm, "end": v(45.48, 25.3) * mm});
            skLineSegment(sketch, "E390", {"start": v(45.48, 25.3) * mm, "end": v(45.48, 25.47) * mm});
            skLineSegment(sketch, "E391", {"start": v(45.48, 25.47) * mm, "end": v(45.96, 25.47) * mm});
            skLineSegment(sketch, "E392", {"start": v(45.96, 25.47) * mm, "end": v(45.96, 25.3) * mm});
            skLineSegment(sketch, "E393", {"start": v(45.96, 25.3) * mm, "end": v(46.25, 25.3) * mm});
            skLineSegment(sketch, "E394", {"start": v(46.25, 25.3) * mm, "end": v(46.25, 23.25) * mm});
            skLineSegment(sketch, "E395", {"start": v(46.25, 23.25) * mm, "end": v(47.55, 23.25) * mm});
            skLineSegment(sketch, "E396", {"start": v(47.55, 23.25) * mm, "end": v(47.55, 25.47) * mm});
            skLineSegment(sketch, "E397", {"start": v(47.55, 25.47) * mm, "end": v(47.31, 25.47) * mm});
            skLineSegment(sketch, "E398", {"start": v(47.31, 25.47) * mm, "end": v(47.31, 25.81) * mm});
            skLineSegment(sketch, "E399", {"start": v(47.31, 25.81) * mm, "end": v(46.95, 25.81) * mm});
            skLineSegment(sketch, "E400", {"start": v(46.95, 25.81) * mm, "end": v(46.95, 25.97) * mm});
            skLineSegment(sketch, "E401", {"start": v(46.95, 25.97) * mm, "end": v(46.12, 25.97) * mm});
            skLineSegment(sketch, "E402", {"start": v(46.12, 25.97) * mm, "end": v(46.12, 25.81) * mm});
            skLineSegment(sketch, "E403", {"start": v(46.12, 25.81) * mm, "end": v(45.33, 25.81) * mm});
            skLineSegment(sketch, "E404", {"start": v(45.33, 25.81) * mm, "end": v(45.33, 25.6) * mm});
            skLineSegment(sketch, "E405", {"start": v(45.33, 25.6) * mm, "end": v(45.15, 25.6) * mm});
            skLineSegment(sketch, "E406", {"start": v(45.15, 25.6) * mm, "end": v(45.15, 25.73) * mm});
            skLineSegment(sketch, "E407", {"start": v(45.15, 25.73) * mm, "end": v(43.97, 25.73) * mm});
            skLineSegment(sketch, "E408", {"start": v(43.97, 25.73) * mm, "end": v(43.97, 23.25) * mm});
            skLineSegment(sketch, "E409", {"start": v(48.7, 23.25) * mm, "end": v(49.73, 23.25) * mm});
            skLineSegment(sketch, "E410", {"start": v(49.73, 23.25) * mm, "end": v(49.73, 25.63) * mm});
            skLineSegment(sketch, "E411", {"start": v(49.73, 25.63) * mm, "end": v(50.55, 25.63) * mm});
            skLineSegment(sketch, "E412", {"start": v(50.55, 25.63) * mm, "end": v(50.55, 26.17) * mm});
            skLineSegment(sketch, "E413", {"start": v(50.55, 26.17) * mm, "end": v(49.92, 26.17) * mm});
            skLineSegment(sketch, "E414", {"start": v(49.92, 26.17) * mm, "end": v(49.92, 26.6) * mm});
            skLineSegment(sketch, "E415", {"start": v(49.92, 26.6) * mm, "end": v(48.76, 26.6) * mm});
            skLineSegment(sketch, "E416", {"start": v(48.76, 26.6) * mm, "end": v(48.76, 26.2) * mm});
            skLineSegment(sketch, "E417", {"start": v(48.76, 26.2) * mm, "end": v(48.04, 26.2) * mm});
            skLineSegment(sketch, "E418", {"start": v(48.04, 26.2) * mm, "end": v(48.04, 25.74) * mm});
            skLineSegment(sketch, "E419", {"start": v(48.04, 25.74) * mm, "end": v(48.7, 25.74) * mm});
            skLineSegment(sketch, "E420", {"start": v(48.7, 25.74) * mm, "end": v(48.7, 23.25) * mm});
            skLineSegment(sketch, "E421", {"start": v(51.97, 24.47) * mm, "end": v(53.83, 24.47) * mm});
            skLineSegment(sketch, "E422", {"start": v(53.83, 24.47) * mm, "end": v(53.83, 24.9) * mm});
            skLineSegment(sketch, "E423", {"start": v(53.83, 24.9) * mm, "end": v(53.65, 24.9) * mm});
            skLineSegment(sketch, "E424", {"start": v(53.65, 24.9) * mm, "end": v(53.65, 25.3) * mm});
            skLineSegment(sketch, "E425", {"start": v(53.65, 25.3) * mm, "end": v(53.45, 25.3) * mm});
            skLineSegment(sketch, "E426", {"start": v(53.45, 25.3) * mm, "end": v(53.45, 25.6) * mm});
            skLineSegment(sketch, "E427", {"start": v(53.45, 25.6) * mm, "end": v(53.27, 25.6) * mm});
            skLineSegment(sketch, "E428", {"start": v(53.27, 25.6) * mm, "end": v(53.27, 25.81) * mm});
            skLineSegment(sketch, "E429", {"start": v(53.27, 25.81) * mm, "end": v(52.76, 25.81) * mm});
            skLineSegment(sketch, "E430", {"start": v(52.76, 25.81) * mm, "end": v(52.76, 25.96) * mm});
            skLineSegment(sketch, "E431", {"start": v(52.76, 25.96) * mm, "end": v(51.8, 25.96) * mm});
            skLineSegment(sketch, "E432", {"start": v(51.8, 25.96) * mm, "end": v(51.8, 25.81) * mm});
            skLineSegment(sketch, "E433", {"start": v(51.8, 25.81) * mm, "end": v(51.3, 25.81) * mm});
            skLineSegment(sketch, "E434", {"start": v(51.3, 25.81) * mm, "end": v(51.3, 25.6) * mm});
            skLineSegment(sketch, "E435", {"start": v(51.3, 25.6) * mm, "end": v(51.02, 25.6) * mm});
            skLineSegment(sketch, "E436", {"start": v(51.02, 25.6) * mm, "end": v(51.02, 25.3) * mm});
            skLineSegment(sketch, "E437", {"start": v(51.02, 25.3) * mm, "end": v(50.81, 25.3) * mm});
            skLineSegment(sketch, "E438", {"start": v(50.81, 25.3) * mm, "end": v(50.81, 24.99) * mm});
            skLineSegment(sketch, "E439", {"start": v(50.81, 24.99) * mm, "end": v(50.52, 24.99) * mm});
            skLineSegment(sketch, "E440", {"start": v(50.52, 24.99) * mm, "end": v(50.52, 24.15) * mm});
            skLineSegment(sketch, "E441", {"start": v(50.52, 24.15) * mm, "end": v(50.75, 24.15) * mm});
            skLineSegment(sketch, "E442", {"start": v(50.75, 24.15) * mm, "end": v(50.75, 23.62) * mm});
            skLineSegment(sketch, "E443", {"start": v(50.75, 23.62) * mm, "end": v(50.95, 23.62) * mm});
            skLineSegment(sketch, "E444", {"start": v(50.95, 23.62) * mm, "end": v(50.95, 23.36) * mm});
            skLineSegment(sketch, "E445", {"start": v(50.95, 23.36) * mm, "end": v(51.17, 23.36) * mm});
            skLineSegment(sketch, "E446", {"start": v(51.17, 23.36) * mm, "end": v(51.17, 23.05) * mm});
            skLineSegment(sketch, "E447", {"start": v(51.17, 23.05) * mm, "end": v(51.56, 23.05) * mm});
            skLineSegment(sketch, "E448", {"start": v(51.56, 23.05) * mm, "end": v(51.56, 22.86) * mm});
            skLineSegment(sketch, "E449", {"start": v(51.56, 22.86) * mm, "end": v(52.96, 22.86) * mm});
            skLineSegment(sketch, "E450", {"start": v(52.96, 22.86) * mm, "end": v(52.96, 23.1) * mm});
            skLineSegment(sketch, "E451", {"start": v(52.96, 23.1) * mm, "end": v(53.44, 23.1) * mm});
            skLineSegment(sketch, "E452", {"start": v(53.44, 23.1) * mm, "end": v(53.44, 23.25) * mm});
            skLineSegment(sketch, "E453", {"start": v(53.44, 23.25) * mm, "end": v(53.68, 23.25) * mm});
            skLineSegment(sketch, "E454", {"start": v(53.68, 23.25) * mm, "end": v(53.68, 23.75) * mm});
            skLineSegment(sketch, "E455", {"start": v(53.68, 23.75) * mm, "end": v(53.92, 23.75) * mm});
            skLineSegment(sketch, "E456", {"start": v(53.92, 23.75) * mm, "end": v(53.92, 24.12) * mm});
            skLineSegment(sketch, "E457", {"start": v(53.92, 24.12) * mm, "end": v(52.76, 24.12) * mm});
            skLineSegment(sketch, "E458", {"start": v(52.76, 24.12) * mm, "end": v(52.76, 23.43) * mm});
            skLineSegment(sketch, "E459", {"start": v(52.76, 23.43) * mm, "end": v(51.95, 23.43) * mm});
            skLineSegment(sketch, "E460", {"start": v(51.95, 23.43) * mm, "end": v(51.97, 24.47) * mm});
            skLineSegment(sketch, "E461", {"start": v(51.97, 24.99) * mm, "end": v(52.65, 24.99) * mm});
            skLineSegment(sketch, "E462", {"start": v(52.65, 24.99) * mm, "end": v(52.65, 25.47) * mm});
            skLineSegment(sketch, "E463", {"start": v(52.65, 25.47) * mm, "end": v(52.47, 25.47) * mm});
            skLineSegment(sketch, "E464", {"start": v(52.47, 25.47) * mm, "end": v(52.47, 25.66) * mm});
            skLineSegment(sketch, "E465", {"start": v(52.47, 25.66) * mm, "end": v(52.17, 25.66) * mm});
            skLineSegment(sketch, "E466", {"start": v(52.17, 25.66) * mm, "end": v(52.17, 25.47) * mm});
            skLineSegment(sketch, "E467", {"start": v(52.17, 25.47) * mm, "end": v(51.97, 25.47) * mm});
            skLineSegment(sketch, "E468", {"start": v(51.97, 25.47) * mm, "end": v(51.97, 24.99) * mm});
            skLineSegment(sketch, "E469", {"start": v(54.36, 25.81) * mm, "end": v(54.36, 23.25) * mm});
            skLineSegment(sketch, "E470", {"start": v(54.36, 23.25) * mm, "end": v(55.36, 23.25) * mm});
            skLineSegment(sketch, "E471", {"start": v(55.36, 23.25) * mm, "end": v(55.36, 24.99) * mm});
            skLineSegment(sketch, "E472", {"start": v(55.36, 24.99) * mm, "end": v(55.64, 24.99) * mm});
            skLineSegment(sketch, "E473", {"start": v(55.64, 24.99) * mm, "end": v(55.64, 25.3) * mm});
            skLineSegment(sketch, "E474", {"start": v(55.64, 25.3) * mm, "end": v(56.28, 25.3) * mm});
            skLineSegment(sketch, "E475", {"start": v(56.28, 25.3) * mm, "end": v(56.28, 24.99) * mm});
            skLineSegment(sketch, "E476", {"start": v(56.28, 24.99) * mm, "end": v(56.62, 24.99) * mm});
            skLineSegment(sketch, "E477", {"start": v(56.62, 24.99) * mm, "end": v(56.62, 23.25) * mm});
            skLineSegment(sketch, "E478", {"start": v(56.62, 23.25) * mm, "end": v(57.7, 23.25) * mm});
            skLineSegment(sketch, "E479", {"start": v(57.7, 23.25) * mm, "end": v(57.7, 25.47) * mm});
            skLineSegment(sketch, "E480", {"start": v(57.7, 25.47) * mm, "end": v(57.48, 25.47) * mm});
            skLineSegment(sketch, "E481", {"start": v(57.48, 25.47) * mm, "end": v(57.48, 25.81) * mm});
            skLineSegment(sketch, "E482", {"start": v(57.48, 25.81) * mm, "end": v(57.27, 25.81) * mm});
            skLineSegment(sketch, "E483", {"start": v(57.27, 25.81) * mm, "end": v(57.27, 26.06) * mm});
            skLineSegment(sketch, "E484", {"start": v(57.27, 26.06) * mm, "end": v(56.04, 26.06) * mm});
            skLineSegment(sketch, "E485", {"start": v(56.04, 26.06) * mm, "end": v(56.04, 25.81) * mm});
            skLineSegment(sketch, "E486", {"start": v(56.04, 25.81) * mm, "end": v(55.56, 25.81) * mm});
            skLineSegment(sketch, "E487", {"start": v(55.56, 25.81) * mm, "end": v(55.56, 25.63) * mm});
            skLineSegment(sketch, "E488", {"start": v(55.56, 25.63) * mm, "end": v(55.34, 25.63) * mm});
            skLineSegment(sketch, "E489", {"start": v(55.34, 25.63) * mm, "end": v(55.34, 25.81) * mm});
            skLineSegment(sketch, "E490", {"start": v(55.34, 25.81) * mm, "end": v(54.36, 25.81) * mm});
            skLineSegment(sketch, "E491", {"start": v(60.65, 27.27) * mm, "end": v(61.61, 27.27) * mm});
            skLineSegment(sketch, "E492", {"start": v(61.61, 27.27) * mm, "end": v(61.61, 23.27) * mm});
            skLineSegment(sketch, "E493", {"start": v(61.61, 23.27) * mm, "end": v(59.12, 23.27) * mm});
            skLineSegment(sketch, "E494", {"start": v(59.12, 23.27) * mm, "end": v(59.12, 23.45) * mm});
            skLineSegment(sketch, "E495", {"start": v(59.12, 23.45) * mm, "end": v(58.56, 23.45) * mm});
            skLineSegment(sketch, "E496", {"start": v(58.56, 23.45) * mm, "end": v(58.56, 23.8) * mm});
            skLineSegment(sketch, "E497", {"start": v(58.56, 23.8) * mm, "end": v(58.21, 23.8) * mm});
            skLineSegment(sketch, "E498", {"start": v(58.21, 23.8) * mm, "end": v(58.21, 25.15) * mm});
            skLineSegment(sketch, "E499", {"start": v(58.21, 25.15) * mm, "end": v(58.5, 25.15) * mm});
            skLineSegment(sketch, "E500", {"start": v(58.5, 25.15) * mm, "end": v(58.5, 25.63) * mm});
            skLineSegment(sketch, "E501", {"start": v(58.5, 25.63) * mm, "end": v(58.77, 25.63) * mm});
            skLineSegment(sketch, "E502", {"start": v(58.77, 25.63) * mm, "end": v(58.77, 25.81) * mm});
            skLineSegment(sketch, "E503", {"start": v(58.77, 25.81) * mm, "end": v(59.12, 25.81) * mm});
            skLineSegment(sketch, "E504", {"start": v(59.12, 25.81) * mm, "end": v(59.12, 26.06) * mm});
            skLineSegment(sketch, "E505", {"start": v(59.12, 26.06) * mm, "end": v(60.65, 26.06) * mm});
            skLineSegment(sketch, "E506", {"start": v(60.65, 26.06) * mm, "end": v(60.65, 27.27) * mm});
            skLineSegment(sketch, "E507", {"start": v(63.23, 25.56) * mm, "end": v(63.67, 25.56) * mm});
            skLineSegment(sketch, "E508", {"start": v(63.67, 25.56) * mm, "end": v(63.95, 25.3) * mm});
            skLineSegment(sketch, "E509", {"start": v(63.95, 25.3) * mm, "end": v(63.95, 23.88) * mm});
            skLineSegment(sketch, "E510", {"start": v(63.95, 23.88) * mm, "end": v(63.67, 23.52) * mm});
            skLineSegment(sketch, "E511", {"start": v(63.67, 23.52) * mm, "end": v(63.23, 23.52) * mm});
            skLineSegment(sketch, "E512", {"start": v(63.23, 23.52) * mm, "end": v(62.95, 23.88) * mm});
            skLineSegment(sketch, "E513", {"start": v(62.95, 23.88) * mm, "end": v(62.95, 25.3) * mm});
            skLineSegment(sketch, "E514", {"start": v(62.95, 25.3) * mm, "end": v(63.23, 25.56) * mm});
            skLineSegment(sketch, "E515", {"start": v(64.2, 25.97) * mm, "end": v(64.2, 25.76) * mm});
            skLineSegment(sketch, "E516", {"start": v(64.2, 25.76) * mm, "end": v(64.73, 25.78) * mm});
            skLineSegment(sketch, "E517", {"start": v(64.73, 25.78) * mm, "end": v(64.75, 25.3) * mm});
            skLineSegment(sketch, "E518", {"start": v(64.75, 25.3) * mm, "end": v(65.08, 25.32) * mm});
            skLineSegment(sketch, "E519", {"start": v(65.08, 25.32) * mm, "end": v(65.12, 23.76) * mm});
            skLineSegment(sketch, "E520", {"start": v(65.12, 23.76) * mm, "end": v(64.78, 23.75) * mm});
            skLineSegment(sketch, "E521", {"start": v(64.78, 23.75) * mm, "end": v(64.78, 23.46) * mm});
            skLineSegment(sketch, "E522", {"start": v(64.78, 23.46) * mm, "end": v(64.47, 23.45) * mm});
            skLineSegment(sketch, "E523", {"start": v(64.47, 23.45) * mm, "end": v(64.48, 23.1) * mm});
            skLineSegment(sketch, "E524", {"start": v(62.31, 23.46) * mm, "end": v(62.31, 23.77) * mm});
            skLineSegment(sketch, "E525", {"start": v(62.31, 23.77) * mm, "end": v(62.08, 23.77) * mm});
            skLineSegment(sketch, "E526", {"start": v(62.08, 23.77) * mm, "end": v(62.08, 25.3) * mm});
            skLineSegment(sketch, "E527", {"start": v(62.08, 25.3) * mm, "end": v(62.43, 25.3) * mm});
            skLineSegment(sketch, "E528", {"start": v(62.43, 25.3) * mm, "end": v(62.43, 25.75) * mm});
            skLineSegment(sketch, "E529", {"start": v(62.43, 25.75) * mm, "end": v(62.8, 25.75) * mm});
            skLineSegment(sketch, "E530", {"start": v(62.8, 25.75) * mm, "end": v(62.8, 25.97) * mm});
            skLineSegment(sketch, "E531", {"start": v(62.8, 25.97) * mm, "end": v(64.2, 25.97) * mm});
            skLineSegment(sketch, "E532", {"start": v(25.01, -13.25) * mm, "end": v(25.01, -10.62) * mm});
            skLineSegment(sketch, "E533", {"start": v(25.01, -10.62) * mm, "end": v(24.86, -10.33) * mm});
            skLineSegment(sketch, "E534", {"start": v(24.86, -10.33) * mm, "end": v(24.5, -10) * mm});
            skLineSegment(sketch, "E535", {"start": v(24.5, -10) * mm, "end": v(24.1, -9.66) * mm});
            skLineSegment(sketch, "E536", {"start": v(24.1, -9.66) * mm, "end": v(-8.63, -9.66) * mm});
            skLineSegment(sketch, "E537", {"start": v(-8.63, -9.66) * mm, "end": v(-9.04, -9.66) * mm});
            skLineSegment(sketch, "E538", {"start": v(-9.04, -9.66) * mm, "end": v(-9.4, -9.94) * mm});
            skLineSegment(sketch, "E539", {"start": v(-9.4, -9.94) * mm, "end": v(-9.67, -10.25) * mm});
            skLineSegment(sketch, "E540", {"start": v(-9.67, -10.25) * mm, "end": v(-9.93, -10.49) * mm});
            skLineSegment(sketch, "E541", {"start": v(-9.93, -10.49) * mm, "end": v(-9.93, -13.25) * mm});
            skLineSegment(sketch, "E542", {"start": v(-42.78, 1.27) * mm, "end": v(-49.91, 1.27) * mm});
            skLineSegment(sketch, "E543", {"start": v(-49.91, 1.27) * mm, "end": v(-50.43, 1.27) * mm});
            skLineSegment(sketch, "E544", {"start": v(-50.43, 1.27) * mm, "end": v(-50.67, 1.46) * mm});
            skLineSegment(sketch, "E545", {"start": v(-50.67, 1.46) * mm, "end": v(-51.19, 2) * mm});
            skLineSegment(sketch, "E546", {"start": v(-51.19, 2) * mm, "end": v(-51.19, 13.89) * mm});
            skLineSegment(sketch, "E547", {"start": v(-51.19, 13.89) * mm, "end": v(-50.92, 14.36) * mm});
            skLineSegment(sketch, "E548", {"start": v(-50.92, 14.36) * mm, "end": v(-50.03, 15) * mm});
            skLineSegment(sketch, "E549", {"start": v(-50.03, 15) * mm, "end": v(-42.59, 15) * mm});
            skLineSegment(sketch, "E550", {"start": v(-42.59, 15) * mm, "end": v(-42.59, 23.2) * mm});
            skLineSegment(sketch, "E551", {"start": v(-42.59, 23.2) * mm, "end": v(-42.32, 23.6) * mm});
            skLineSegment(sketch, "E552", {"start": v(-42.32, 23.6) * mm, "end": v(-41.84, 24.1) * mm});
            skLineSegment(sketch, "E553", {"start": v(-41.84, 24.1) * mm, "end": v(-41.33, 24.35) * mm});
            skLineSegment(sketch, "E554", {"start": v(-41.33, 24.35) * mm, "end": v(-41.08, 24.43) * mm});
            skLineSegment(sketch, "E555", {"start": v(-41.08, 24.43) * mm, "end": v(-28.91, 24.43) * mm});
            skLineSegment(sketch, "E556", {"start": v(-28.91, 24.43) * mm, "end": v(-28.48, 24.46) * mm});
            skLineSegment(sketch, "E557", {"start": v(-28.48, 24.46) * mm, "end": v(-28.23, 24.3) * mm});
            skLineSegment(sketch, "E558", {"start": v(-28.23, 24.3) * mm, "end": v(-27.86, 24) * mm});
            skLineSegment(sketch, "E559", {"start": v(-27.86, 24) * mm, "end": v(-27.57, 23.72) * mm});
            skLineSegment(sketch, "E560", {"start": v(-27.57, 23.72) * mm, "end": v(-27.57, 15.23) * mm});
            skLineSegment(sketch, "E561", {"start": v(-27.57, 15.23) * mm, "end": v(-20.54, 15.23) * mm});
            skLineSegment(sketch, "E562", {"start": v(-20.54, 15.23) * mm, "end": v(-20.15, 15.06) * mm});
            skLineSegment(sketch, "E563", {"start": v(-20.15, 15.06) * mm, "end": v(-19.62, 14.54) * mm});
            skLineSegment(sketch, "E564", {"start": v(-19.62, 14.54) * mm, "end": v(-19.29, 14.13) * mm});
            skLineSegment(sketch, "E565", {"start": v(-19.29, 14.13) * mm, "end": v(-19.06, 13.72) * mm});
            skLineSegment(sketch, "E566", {"start": v(-19.06, 13.72) * mm, "end": v(-19.06, 2.72) * mm});
            skLineSegment(sketch, "E567", {"start": v(-19.06, 2.72) * mm, "end": v(-19.21, 2.14) * mm});
            skLineSegment(sketch, "E568", {"start": v(-19.21, 2.14) * mm, "end": v(-19.54, 1.85) * mm});
            skLineSegment(sketch, "E569", {"start": v(-19.54, 1.85) * mm, "end": v(-19.97, 1.34) * mm});
            skLineSegment(sketch, "E570", {"start": v(-19.97, 1.34) * mm, "end": v(-20.67, 0.97) * mm});
            skLineSegment(sketch, "E571", {"start": v(-20.67, 0.97) * mm, "end": v(-27.25, 0.97) * mm});
            skLineSegment(sketch, "E572", {"start": v(-27.25, 0.97) * mm, "end": v(-27.25, -7.17) * mm});
            skLineSegment(sketch, "E573", {"start": v(-27.25, -7.17) * mm, "end": v(-27.33, -7.54) * mm});
            skLineSegment(sketch, "E574", {"start": v(-27.33, -7.54) * mm, "end": v(-27.58, -7.85) * mm});
            skLineSegment(sketch, "E575", {"start": v(-27.58, -7.85) * mm, "end": v(-27.88, -8.26) * mm});
            skLineSegment(sketch, "E576", {"start": v(-27.88, -8.26) * mm, "end": v(-28.3, -8.53) * mm});
            skLineSegment(sketch, "E577", {"start": v(-28.3, -8.53) * mm, "end": v(-41.48, -8.53) * mm});
            skLineSegment(sketch, "E578", {"start": v(-41.48, -8.53) * mm, "end": v(-41.9, -8.58) * mm});
            skLineSegment(sketch, "E579", {"start": v(-41.9, -8.58) * mm, "end": v(-42.22, -8.43) * mm});
            skLineSegment(sketch, "E580", {"start": v(-42.22, -8.43) * mm, "end": v(-42.6, -8.17) * mm});
            skLineSegment(sketch, "E581", {"start": v(-42.6, -8.17) * mm, "end": v(-42.78, -7.96) * mm});
            skLineSegment(sketch, "E582", {"start": v(-42.78, -7.96) * mm, "end": v(-42.78, 1.27) * mm});
            skLineSegment(sketch, "E583", {"start": v(-9.86, 40.98) * mm, "end": v(-9.86, 35.56) * mm});
            skLineSegment(sketch, "E584", {"start": v(-9.86, 35.56) * mm, "end": v(-9.6, 35.01) * mm});
            skLineSegment(sketch, "E585", {"start": v(-9.6, 35.01) * mm, "end": v(-9.32, 34.66) * mm});
            skLineSegment(sketch, "E586", {"start": v(-9.32, 34.66) * mm, "end": v(-8.93, 34.24) * mm});
            skLineSegment(sketch, "E587", {"start": v(-8.93, 34.24) * mm, "end": v(23.52, 34.24) * mm});
            skLineSegment(sketch, "E588", {"start": v(23.52, 34.24) * mm, "end": v(24.24, 34.38) * mm});
            skLineSegment(sketch, "E589", {"start": v(24.24, 34.38) * mm, "end": v(24.57, 34.6) * mm});
            skLineSegment(sketch, "E590", {"start": v(24.57, 34.6) * mm, "end": v(25, 35.04) * mm});
            skLineSegment(sketch, "E591", {"start": v(25, 35.04) * mm, "end": v(25, 40.98) * mm});
            skLineSegment(sketch, "E592", {"start": v(-8.67, 29.97) * mm, "end": v(23.5, 29.97) * mm});
            skLineSegment(sketch, "E593", {"start": v(23.5, 29.97) * mm, "end": v(24.15, 29.91) * mm});
            skLineSegment(sketch, "E594", {"start": v(24.15, 29.91) * mm, "end": v(24.46, 29.81) * mm});
            skLineSegment(sketch, "E595", {"start": v(24.46, 29.81) * mm, "end": v(25.08, 29.19) * mm});
            skLineSegment(sketch, "E596", {"start": v(25.08, 29.19) * mm, "end": v(25.34, 28.9) * mm});
            skLineSegment(sketch, "E597", {"start": v(25.34, 28.9) * mm, "end": v(25.34, 23) * mm});
            skLineSegment(sketch, "E598", {"start": v(25.34, 23) * mm, "end": v(25.29, 22.6) * mm});
            skLineSegment(sketch, "E599", {"start": v(25.29, 22.6) * mm, "end": v(25.03, 22.33) * mm});
            skLineSegment(sketch, "E600", {"start": v(25.03, 22.33) * mm, "end": v(24.58, 21.9) * mm});
            skLineSegment(sketch, "E601", {"start": v(24.58, 21.9) * mm, "end": v(24.25, 21.76) * mm});
            skLineSegment(sketch, "E602", {"start": v(24.25, 21.76) * mm, "end": v(-8.67, 21.76) * mm});
            skLineSegment(sketch, "E603", {"start": v(-8.67, 21.76) * mm, "end": v(-9.06, 21.76) * mm});
            skLineSegment(sketch, "E604", {"start": v(-9.06, 21.76) * mm, "end": v(-9.4, 22) * mm});
            skLineSegment(sketch, "E605", {"start": v(-9.4, 22) * mm, "end": v(-9.79, 22.49) * mm});
            skLineSegment(sketch, "E606", {"start": v(-9.79, 22.49) * mm, "end": v(-9.92, 22.67) * mm});
            skLineSegment(sketch, "E607", {"start": v(-9.92, 22.67) * mm, "end": v(-9.92, 28.6) * mm});
            skLineSegment(sketch, "E608", {"start": v(-9.92, 28.6) * mm, "end": v(-9.78, 29) * mm});
            skLineSegment(sketch, "E609", {"start": v(-9.78, 29) * mm, "end": v(-9.4, 29.5) * mm});
            skLineSegment(sketch, "E610", {"start": v(-9.4, 29.5) * mm, "end": v(-9.08, 29.81) * mm});
            skLineSegment(sketch, "E611", {"start": v(-9.08, 29.81) * mm, "end": v(-8.67, 29.97) * mm});
            skLineSegment(sketch, "E612", {"start": v(88.83, 39.45) * mm, "end": v(88.83, -11.98) * mm});
            skLineSegment(sketch, "E613", {"start": v(-8.67, 17.54) * mm, "end": v(23.56, 17.54) * mm});
            skLineSegment(sketch, "E614", {"start": v(23.56, 17.54) * mm, "end": v(24.2, 17.44) * mm});
            skLineSegment(sketch, "E615", {"start": v(24.2, 17.44) * mm, "end": v(24.85, 17.1) * mm});
            skLineSegment(sketch, "E616", {"start": v(24.85, 17.1) * mm, "end": v(25.28, 16.54) * mm});
            skLineSegment(sketch, "E617", {"start": v(25.28, 16.54) * mm, "end": v(25.28, 10.68) * mm});
            skLineSegment(sketch, "E618", {"start": v(25.28, 10.68) * mm, "end": v(25, 9.94) * mm});
            skLineSegment(sketch, "E619", {"start": v(25, 9.94) * mm, "end": v(24.6, 9.6) * mm});
            skLineSegment(sketch, "E620", {"start": v(24.6, 9.6) * mm, "end": v(24.2, 9.35) * mm});
            skLineSegment(sketch, "E621", {"start": v(24.2, 9.35) * mm, "end": v(-8.67, 9.35) * mm});
            skLineSegment(sketch, "E622", {"start": v(-8.67, 9.35) * mm, "end": v(-9.04, 9.35) * mm});
            skLineSegment(sketch, "E623", {"start": v(-9.04, 9.35) * mm, "end": v(-9.53, 9.7) * mm});
            skLineSegment(sketch, "E624", {"start": v(-9.53, 9.7) * mm, "end": v(-9.86, 10.02) * mm});
            skLineSegment(sketch, "E625", {"start": v(-9.86, 10.02) * mm, "end": v(-9.86, 16.24) * mm});
            skLineSegment(sketch, "E626", {"start": v(-9.86, 16.24) * mm, "end": v(-9.66, 16.76) * mm});
            skLineSegment(sketch, "E627", {"start": v(-9.66, 16.76) * mm, "end": v(-9.32, 17.16) * mm});
            skLineSegment(sketch, "E628", {"start": v(-9.32, 17.16) * mm, "end": v(-8.67, 17.54) * mm});
            skLineSegment(sketch, "E629", {"start": v(-5.05, 0.44) * mm, "end": v(3.62, 0.44) * mm});
            skLineSegment(sketch, "E630", {"start": v(3.62, 0.44) * mm, "end": v(3.86, 0.38) * mm});
            skLineSegment(sketch, "E631", {"start": v(3.86, 0.38) * mm, "end": v(4.12, 0.22) * mm});
            skLineSegment(sketch, "E632", {"start": v(4.12, 0.22) * mm, "end": v(4.47, -0.07) * mm});
            skLineSegment(sketch, "E633", {"start": v(4.47, -0.07) * mm, "end": v(4.66, -0.33) * mm});
            skLineSegment(sketch, "E634", {"start": v(4.66, -0.33) * mm, "end": v(4.83, -0.63) * mm});
            skLineSegment(sketch, "E635", {"start": v(4.83, -0.63) * mm, "end": v(4.83, -1.9) * mm});
            skLineSegment(sketch, "E636", {"start": v(4.83, -1.9) * mm, "end": v(4.68, -2.2) * mm});
            skLineSegment(sketch, "E637", {"start": v(4.68, -2.2) * mm, "end": v(4.5, -2.52) * mm});
            skLineSegment(sketch, "E638", {"start": v(4.5, -2.52) * mm, "end": v(4.16, -2.84) * mm});
            skLineSegment(sketch, "E639", {"start": v(4.16, -2.84) * mm, "end": v(3.76, -3.07) * mm});
            skLineSegment(sketch, "E640", {"start": v(3.76, -3.07) * mm, "end": v(-4.8, -3.07) * mm});
            skLineSegment(sketch, "E641", {"start": v(-4.8, -3.07) * mm, "end": v(-5.17, -3.07) * mm});
            skLineSegment(sketch, "E642", {"start": v(-5.17, -3.07) * mm, "end": v(-5.42, -2.85) * mm});
            skLineSegment(sketch, "E643", {"start": v(-5.42, -2.85) * mm, "end": v(-5.73, -2.6) * mm});
            skLineSegment(sketch, "E644", {"start": v(-5.73, -2.6) * mm, "end": v(-6.02, -2.4) * mm});
            skLineSegment(sketch, "E645", {"start": v(-6.02, -2.4) * mm, "end": v(-6.02, -0.8) * mm});
            skLineSegment(sketch, "E646", {"start": v(-6.02, -0.8) * mm, "end": v(-5.87, -0.43) * mm});
            skLineSegment(sketch, "E647", {"start": v(-5.87, -0.43) * mm, "end": v(-5.55, -0.08) * mm});
            skLineSegment(sketch, "E648", {"start": v(-5.55, -0.08) * mm, "end": v(-5.36, 0.16) * mm});
            skLineSegment(sketch, "E649", {"start": v(-5.36, 0.16) * mm, "end": v(-5.05, 0.44) * mm});
            skLineSegment(sketch, "E650", {"start": v(-8.9, 6.59) * mm, "end": v(23.94, 6.59) * mm});
            skLineSegment(sketch, "E651", {"start": v(23.94, 6.59) * mm, "end": v(24.48, 6.5) * mm});
            skLineSegment(sketch, "E652", {"start": v(24.48, 6.5) * mm, "end": v(25.02, 6.21) * mm});
            skLineSegment(sketch, "E653", {"start": v(25.02, 6.21) * mm, "end": v(25.33, 5.8) * mm});
            skLineSegment(sketch, "E654", {"start": v(25.33, 5.8) * mm, "end": v(25.53, 5.45) * mm});
            skLineSegment(sketch, "E655", {"start": v(25.53, 5.45) * mm, "end": v(25.53, -6.08) * mm});
            skLineSegment(sketch, "E656", {"start": v(25.53, -6.08) * mm, "end": v(25.37, -6.45) * mm});
            skLineSegment(sketch, "E657", {"start": v(25.37, -6.45) * mm, "end": v(24.93, -6.9) * mm});
            skLineSegment(sketch, "E658", {"start": v(24.93, -6.9) * mm, "end": v(24.52, -7.13) * mm});
            skLineSegment(sketch, "E659", {"start": v(24.52, -7.13) * mm, "end": v(23.82, -7.5) * mm});
            skLineSegment(sketch, "E660", {"start": v(23.82, -7.5) * mm, "end": v(-9.23, -7.5) * mm});
            skLineSegment(sketch, "E661", {"start": v(-9.23, -7.5) * mm, "end": v(-9.6, -7.5) * mm});
            skLineSegment(sketch, "E662", {"start": v(-9.6, -7.5) * mm, "end": v(-9.85, -7.23) * mm});
            skLineSegment(sketch, "E663", {"start": v(-9.85, -7.23) * mm, "end": v(-10.09, -6.97) * mm});
            skLineSegment(sketch, "E664", {"start": v(-10.09, -6.97) * mm, "end": v(-10.3, -6.64) * mm});
            skLineSegment(sketch, "E665", {"start": v(-10.3, -6.64) * mm, "end": v(-10.3, 5.06) * mm});
            skLineSegment(sketch, "E666", {"start": v(-10.3, 5.06) * mm, "end": v(-10.1, 5.67) * mm});
            skLineSegment(sketch, "E667", {"start": v(-10.1, 5.67) * mm, "end": v(-9.62, 6.2) * mm});
            skLineSegment(sketch, "E668", {"start": v(-9.62, 6.2) * mm, "end": v(-8.9, 6.59) * mm});
            skLineSegment(sketch, "E669", {"start": v(-19.62, 49.1) * mm, "end": v(-19.62, 47.2) * mm});
            skLineSegment(sketch, "E670", {"start": v(-19.62, 47.2) * mm, "end": v(-13.78, 47.2) * mm});
            skLineSegment(sketch, "E671", {"start": v(-13.78, 47.2) * mm, "end": v(-13.78, 49.1) * mm});
            skLineSegment(sketch, "E672", {"start": v(-8.9, 5.7) * mm, "end": v(24.04, 5.76) * mm});
            skLineSegment(sketch, "E673", {"start": v(24.04, 5.76) * mm, "end": v(24.45, 5.67) * mm});
            skLineSegment(sketch, "E674", {"start": v(24.45, 5.67) * mm, "end": v(24.76, 5.3) * mm});
            skLineSegment(sketch, "E675", {"start": v(24.76, 5.3) * mm, "end": v(24.89, 5.07) * mm});
            skLineSegment(sketch, "E676", {"start": v(24.89, 5.07) * mm, "end": v(24.9, -6.12) * mm});
            skLineSegment(sketch, "E677", {"start": v(24.9, -6.12) * mm, "end": v(24.75, -6.46) * mm});
            skLineSegment(sketch, "E678", {"start": v(24.75, -6.46) * mm, "end": v(24.33, -6.78) * mm});
            skLineSegment(sketch, "E679", {"start": v(24.33, -6.78) * mm, "end": v(23.96, -7) * mm});
            skLineSegment(sketch, "E680", {"start": v(23.96, -7) * mm, "end": v(-8.9, -7) * mm});
            skLineSegment(sketch, "E681", {"start": v(-8.9, -7) * mm, "end": v(-9.25, -6.94) * mm});
            skLineSegment(sketch, "E682", {"start": v(-9.25, -6.94) * mm, "end": v(-9.52, -6.8) * mm});
            skLineSegment(sketch, "E683", {"start": v(-9.52, -6.8) * mm, "end": v(-9.7, -6.65) * mm});
            skLineSegment(sketch, "E684", {"start": v(-9.7, -6.65) * mm, "end": v(-9.72, 4.8) * mm});
            skLineSegment(sketch, "E685", {"start": v(-9.72, 4.8) * mm, "end": v(-9.62, 5.17) * mm});
            skLineSegment(sketch, "E686", {"start": v(-9.62, 5.17) * mm, "end": v(-9.36, 5.47) * mm});
            skLineSegment(sketch, "E687", {"start": v(-9.36, 5.47) * mm, "end": v(-8.9, 5.7) * mm});
            skLineSegment(sketch, "E688", {"start": v(-40.68, 13.89) * mm, "end": v(-40.7, 22.53) * mm});
            skLineSegment(sketch, "E689", {"start": v(-40.7, 22.53) * mm, "end": v(-29.4, 22.53) * mm});
            skLineSegment(sketch, "E690", {"start": v(-29.4, 22.53) * mm, "end": v(-29.4, 13.89) * mm});
            skLineSegment(sketch, "E691", {"start": v(-29.4, 13.89) * mm, "end": v(-20.7, 13.89) * mm});
            skLineSegment(sketch, "E692", {"start": v(-20.7, 13.89) * mm, "end": v(-20.7, 2.6) * mm});
            skLineSegment(sketch, "E693", {"start": v(-20.7, 2.6) * mm, "end": v(-29.46, 2.6) * mm});
            skLineSegment(sketch, "E694", {"start": v(-29.46, 2.6) * mm, "end": v(-29.45, -7.12) * mm});
            skLineSegment(sketch, "E695", {"start": v(-29.45, -7.12) * mm, "end": v(-40.68, -7.12) * mm});
            skLineSegment(sketch, "E696", {"start": v(-40.68, -7.12) * mm, "end": v(-40.7, 2.48) * mm});
            skLineSegment(sketch, "E697", {"start": v(-40.7, 2.48) * mm, "end": v(-49.98, 2.48) * mm});
            skLineSegment(sketch, "E698", {"start": v(-49.98, 2.48) * mm, "end": v(-49.98, 13.89) * mm});
            skLineSegment(sketch, "E699", {"start": v(-49.98, 13.89) * mm, "end": v(-40.68, 13.89) * mm});
            skLineSegment(sketch, "E700", {"start": v(-36.46, 13.66) * mm, "end": v(-33.2, 13.66) * mm});
            skLineSegment(sketch, "E701", {"start": v(-33.2, 13.66) * mm, "end": v(-33.21, 17.35) * mm});
            skLineSegment(sketch, "E702", {"start": v(-33.21, 17.35) * mm, "end": v(-31.36, 17.35) * mm});
            skLineSegment(sketch, "E703", {"start": v(-31.36, 17.35) * mm, "end": v(-34.84, 20.41) * mm});
            skLineSegment(sketch, "E704", {"start": v(-34.84, 20.41) * mm, "end": v(-38.53, 17.35) * mm});
            skLineSegment(sketch, "E705", {"start": v(-38.53, 17.35) * mm, "end": v(-36.46, 17.35) * mm});
            skLineSegment(sketch, "E706", {"start": v(-36.46, 17.35) * mm, "end": v(-36.46, 13.66) * mm});
            skLineSegment(sketch, "E707", {"start": v(-24.84, 8.87) * mm, "end": v(-24.85, 10.7) * mm});
            skLineSegment(sketch, "E708", {"start": v(-24.85, 10.7) * mm, "end": v(-21.6, 7.7) * mm});
            skLineSegment(sketch, "E709", {"start": v(-21.6, 7.7) * mm, "end": v(-24.84, 4.17) * mm});
            skLineSegment(sketch, "E710", {"start": v(-24.84, 4.17) * mm, "end": v(-24.85, 6.12) * mm});
            skLineSegment(sketch, "E711", {"start": v(-24.85, 6.12) * mm, "end": v(-28.64, 6.12) * mm});
            skLineSegment(sketch, "E712", {"start": v(-28.64, 6.12) * mm, "end": v(-28.64, 8.87) * mm});
            skLineSegment(sketch, "E713", {"start": v(-28.64, 8.87) * mm, "end": v(-24.84, 8.87) * mm});
            skLineSegment(sketch, "E714", {"start": v(-45, 8.87) * mm, "end": v(-45, 10.95) * mm});
            skLineSegment(sketch, "E715", {"start": v(-45, 10.95) * mm, "end": v(-48.25, 7.47) * mm});
            skLineSegment(sketch, "E716", {"start": v(-48.25, 7.47) * mm, "end": v(-44.95, 3.96) * mm});
            skLineSegment(sketch, "E717", {"start": v(-44.95, 3.96) * mm, "end": v(-44.95, 5.75) * mm});
            skLineSegment(sketch, "E718", {"start": v(-44.95, 5.75) * mm, "end": v(-41.08, 5.76) * mm});
            skLineSegment(sketch, "E719", {"start": v(-41.08, 5.76) * mm, "end": v(-41.08, 8.87) * mm});
            skLineSegment(sketch, "E720", {"start": v(-41.08, 8.87) * mm, "end": v(-45, 8.87) * mm});
            skLineSegment(sketch, "E721", {"start": v(-36.04, 1.51) * mm, "end": v(-32.97, 1.51) * mm});
            skLineSegment(sketch, "E722", {"start": v(-32.97, 1.51) * mm, "end": v(-32.97, -1.94) * mm});
            skLineSegment(sketch, "E723", {"start": v(-32.97, -1.94) * mm, "end": v(-31.18, -1.94) * mm});
            skLineSegment(sketch, "E724", {"start": v(-31.18, -1.94) * mm, "end": v(-34.85, -5.5) * mm});
            skLineSegment(sketch, "E725", {"start": v(-34.85, -5.5) * mm, "end": v(-37.94, -2.3) * mm});
            skLineSegment(sketch, "E726", {"start": v(-37.94, -2.3) * mm, "end": v(-36.04, -2.3) * mm});
            skLineSegment(sketch, "E727", {"start": v(-36.04, -2.3) * mm, "end": v(-36.04, 1.51) * mm});
            skLineSegment(sketch, "E728", {"start": v(11.21, 0.22) * mm, "end": v(20.05, 0.22) * mm});
            skLineSegment(sketch, "E729", {"start": v(20.05, 0.22) * mm, "end": v(20.43, 0.13) * mm});
            skLineSegment(sketch, "E730", {"start": v(20.43, 0.13) * mm, "end": v(20.7, -0.14) * mm});
            skLineSegment(sketch, "E731", {"start": v(20.7, -0.14) * mm, "end": v(20.98, -0.45) * mm});
            skLineSegment(sketch, "E732", {"start": v(20.98, -0.45) * mm, "end": v(20.99, -2.33) * mm});
            skLineSegment(sketch, "E733", {"start": v(20.99, -2.33) * mm, "end": v(20.85, -2.8) * mm});
            skLineSegment(sketch, "E734", {"start": v(20.85, -2.8) * mm, "end": v(20.54, -3.12) * mm});
            skLineSegment(sketch, "E735", {"start": v(20.54, -3.12) * mm, "end": v(11.21, -3.13) * mm});
            skLineSegment(sketch, "E736", {"start": v(11.21, -3.13) * mm, "end": v(10.88, -3.07) * mm});
            skLineSegment(sketch, "E737", {"start": v(10.88, -3.07) * mm, "end": v(10.58, -2.8) * mm});
            skLineSegment(sketch, "E738", {"start": v(10.58, -2.8) * mm, "end": v(10.3, -2.61) * mm});
            skLineSegment(sketch, "E739", {"start": v(10.3, -2.61) * mm, "end": v(10.3, -0.72) * mm});
            skLineSegment(sketch, "E740", {"start": v(10.3, -0.72) * mm, "end": v(10.46, -0.3) * mm});
            skLineSegment(sketch, "E741", {"start": v(10.46, -0.3) * mm, "end": v(10.8, 0.01) * mm});
            skLineSegment(sketch, "E742", {"start": v(10.8, 0.01) * mm, "end": v(11.21, 0.22) * mm});
            skLineSegment(sketch, "E743", {"start": v(-2.94, 15.14) * mm, "end": v(-2.89, 15.14) * mm});
            skLineSegment(sketch, "E744", {"start": v(-5.3, 15.14) * mm, "end": v(-5.3, 15.14) * mm});
            skLineSegment(sketch, "E745", {"start": v(59.68, 25.3) * mm, "end": v(60.95, 25.3) * mm});
            skLineSegment(sketch, "E746", {"start": v(60.95, 25.3) * mm, "end": v(60.95, 23.92) * mm});
            skLineSegment(sketch, "E747", {"start": v(60.95, 23.92) * mm, "end": v(59.68, 23.92) * mm});
            skLineSegment(sketch, "E748", {"start": v(59.68, 23.92) * mm, "end": v(59.68, 25.3) * mm});
            skLineSegment(sketch, "E749", {"start": v(64.48, 23.1) * mm, "end": v(62.62, 23.1) * mm});
            skLineSegment(sketch, "E750", {"start": v(62.62, 23.1) * mm, "end": v(62.62, 23.46) * mm});
            skLineSegment(sketch, "E751", {"start": v(62.62, 23.46) * mm, "end": v(62.31, 23.46) * mm});
            skSolve(sketch);
        }
        {
            var Q0;
            Q0=makeQuery(id+"F0.imprint","IMPRINT",FACE,{"disambiguationData":[TD([[makeQuery(id+"F0.imprint","IMPRINT",EDGE,{"derivedFrom":sQuery(id+"F0.wireOp",EDGE,"E700")}),1.0]])]});
            var Q1;
            Q1=makeQuery(id+"F0.imprint","IMPRINT",FACE,{"disambiguationData":[TD([[makeQuery(id+"F0.imprint","IMPRINT",EDGE,{"derivedFrom":sQuery(id+"F0.wireOp",EDGE,"E1")}),-1.0]])]});
            var Q2;
            Q2=makeQuery(id+"F0.imprint","IMPRINT",FACE,{"disambiguationData":[TD([[makeQuery(id+"F0.imprint","IMPRINT",EDGE,{"derivedFrom":sQuery(id+"F0.wireOp",EDGE,"E120")}),-1.0]])]});
            var Q3;
            {var subQ0=sQuery(id+"F0.wireOp",EDGE,"E532");Q3=makeQuery(id+"F0.imprint","IMPRINT",FACE,{"disambiguationData":[TD([[makeQuery(id+"F0.imprint","IMPRINT",EDGE,{"derivedFrom":subQ0}),1.0]])]});}
            var Q4;
            Q4=makeQuery(id+"F0.imprint","IMPRINT",FACE,{"disambiguationData":[TD([[makeQuery(id+"F0.imprint","IMPRINT",EDGE,{"derivedFrom":sQuery(id+"F0.wireOp",EDGE,"E707")}),-1.0]])]});
            var Q5;
            {var subQ0=sQuery(id+"F0.wireOp",EDGE,"E583");Q5=makeQuery(id+"F0.imprint","IMPRINT",FACE,{"disambiguationData":[TD([[makeQuery(id+"F0.imprint","IMPRINT",EDGE,{"derivedFrom":subQ0}),1.0]])]});}
            var Q6;
            Q6=makeQuery(id+"F0.imprint","IMPRINT",FACE,{"disambiguationData":[TD([[makeQuery(id+"F0.imprint","IMPRINT",EDGE,{"derivedFrom":sQuery(id+"F0.wireOp",EDGE,"E121")}),-1.0]])]});
            var Q7;
            Q7=makeQuery(id+"F0.imprint","IMPRINT",FACE,{"disambiguationData":[TD([[makeQuery(id+"F0.imprint","IMPRINT",EDGE,{"derivedFrom":sQuery(id+"F0.wireOp",EDGE,"E714")}),1.0]])]});
            var Q8;
            Q8=makeQuery(id+"F0.imprint","IMPRINT",FACE,{"disambiguationData":[TD([[makeQuery(id+"F0.imprint","IMPRINT",EDGE,{"derivedFrom":sQuery(id+"F0.wireOp",EDGE,"E50")}),1.0]])]});
            var Q9;
            Q9=makeQuery(id+"F0.imprint","IMPRINT",FACE,{"disambiguationData":[TD([[makeQuery(id+"F0.imprint","IMPRINT",EDGE,{"derivedFrom":sQuery(id+"F0.wireOp",EDGE,"E728")}),-1.0]])]});
            var Q10;
            Q10=makeQuery(id+"F0.imprint","IMPRINT",FACE,{"disambiguationData":[TD([[makeQuery(id+"F0.imprint","IMPRINT",EDGE,{"derivedFrom":sQuery(id+"F0.wireOp",EDGE,"E721")}),-1.0]])]});
            var Q11;
            Q11=makeQuery(id+"F0.imprint","IMPRINT",FACE,{"disambiguationData":[TD([[makeQuery(id+"F0.imprint","IMPRINT",EDGE,{"derivedFrom":sQuery(id+"F0.wireOp",EDGE,"E6")}),-1.0]])]});
            var Q12;
            Q12=makeQuery(id+"F0.imprint","IMPRINT",FACE,{"disambiguationData":[TD([[makeQuery(id+"F0.imprint","IMPRINT",EDGE,{"derivedFrom":sQuery(id+"F0.wireOp",EDGE,"E542")}),-1.0]])]});
            var Q13;
            Q13=makeQuery(id+"F0.imprint","IMPRINT",FACE,{"disambiguationData":[TD([[makeQuery(id+"F0.imprint","IMPRINT",EDGE,{"derivedFrom":sQuery(id+"F0.wireOp",EDGE,"E650")}),-1.0]])]});
            var Q14;
            Q14=makeQuery(id+"F0.imprint","IMPRINT",FACE,{"disambiguationData":[TD([[makeQuery(id+"F0.imprint","IMPRINT",EDGE,{"derivedFrom":sQuery(id+"F0.wireOp",EDGE,"E592")}),-1.0]])]});
            var Q15;
            Q15=makeQuery(id+"F0.imprint","IMPRINT",FACE,{"disambiguationData":[TD([[makeQuery(id+"F0.imprint","IMPRINT",EDGE,{"derivedFrom":sQuery(id+"F0.wireOp",EDGE,"E629")}),1.0]])]});
            var Q16;
            Q16=makeQuery(id+"F0.imprint","IMPRINT",FACE,{"disambiguationData":[TD([[makeQuery(id+"F0.imprint","IMPRINT",EDGE,{"derivedFrom":sQuery(id+"F0.wireOp",EDGE,"E629")}),-1.0]])]});
            var Q17;
            Q17=makeQuery(id+"F0.imprint","IMPRINT",FACE,{"disambiguationData":[TD([[makeQuery(id+"F0.imprint","IMPRINT",EDGE,{"derivedFrom":sQuery(id+"F0.wireOp",EDGE,"E51")}),1.0]])]});
            var Q18;
            {var subQ0=sQuery(id+"F0.wireOp",EDGE,"E669");Q18=makeQuery(id+"F0.imprint","IMPRINT",FACE,{"disambiguationData":[TD([[makeQuery(id+"F0.imprint","IMPRINT",EDGE,{"derivedFrom":subQ0}),1.0]])]});}
            var Q19;
            Q19=makeQuery(id+"F0.imprint","IMPRINT",FACE,{"disambiguationData":[TD([[makeQuery(id+"F0.imprint","IMPRINT",EDGE,{"derivedFrom":sQuery(id+"F0.wireOp",EDGE,"E120")}),1.0]])]});
            var Q20;
            Q20=makeQuery(id+"F0.imprint","IMPRINT",FACE,{"disambiguationData":[TD([[makeQuery(id+"F0.imprint","IMPRINT",EDGE,{"derivedFrom":sQuery(id+"F0.wireOp",EDGE,"E369")}),1.0]])]});
            var Q21;
            Q21=makeQuery(id+"F0.imprint","IMPRINT",FACE,{"disambiguationData":[TD([[makeQuery(id+"F0.imprint","IMPRINT",EDGE,{"derivedFrom":sQuery(id+"F0.wireOp",EDGE,"E387")}),1.0]])]});
            var Q22;
            Q22=makeQuery(id+"F0.imprint","IMPRINT",FACE,{"disambiguationData":[TD([[makeQuery(id+"F0.imprint","IMPRINT",EDGE,{"derivedFrom":sQuery(id+"F0.wireOp",EDGE,"E409")}),1.0]])]});
            var Q23;
            Q23=makeQuery(id+"F0.imprint","IMPRINT",FACE,{"disambiguationData":[TD([[makeQuery(id+"F0.imprint","IMPRINT",EDGE,{"derivedFrom":sQuery(id+"F0.wireOp",EDGE,"E491")}),-1.0]])]});
            var Q24;
            Q24=makeQuery(id+"F0.imprint","IMPRINT",FACE,{"disambiguationData":[TD([[makeQuery(id+"F0.imprint","IMPRINT",EDGE,{"derivedFrom":sQuery(id+"F0.wireOp",EDGE,"E361")}),1.0]])]});
            var Q25;
            Q25=makeQuery(id+"F0.imprint","IMPRINT",FACE,{"disambiguationData":[TD([[makeQuery(id+"F0.imprint","IMPRINT",EDGE,{"derivedFrom":sQuery(id+"F0.wireOp",EDGE,"E379")}),1.0]])]});
            var Q26;
            Q26=makeQuery(id+"F0.imprint","IMPRINT",FACE,{"disambiguationData":[TD([[makeQuery(id+"F0.imprint","IMPRINT",EDGE,{"derivedFrom":sQuery(id+"F0.wireOp",EDGE,"E231")}),1.0]])]});
            var Q27;
            Q27=makeQuery(id+"F0.imprint","IMPRINT",FACE,{"disambiguationData":[TD([[makeQuery(id+"F0.imprint","IMPRINT",EDGE,{"derivedFrom":sQuery(id+"F0.wireOp",EDGE,"E90")}),1.0]])]});
            var Q28;
            Q28=makeQuery(id+"F0.imprint","IMPRINT",FACE,{"disambiguationData":[TD([[makeQuery(id+"F0.imprint","IMPRINT",EDGE,{"derivedFrom":sQuery(id+"F0.wireOp",EDGE,"E297")}),1.0]])]});
            var Q29;
            Q29=makeQuery(id+"F0.imprint","IMPRINT",FACE,{"disambiguationData":[TD([[makeQuery(id+"F0.imprint","IMPRINT",EDGE,{"derivedFrom":sQuery(id+"F0.wireOp",EDGE,"E383")}),1.0]])]});
            var Q30;
            Q30=makeQuery(id+"F0.imprint","IMPRINT",FACE,{"disambiguationData":[TD([[makeQuery(id+"F0.imprint","IMPRINT",EDGE,{"derivedFrom":sQuery(id+"F0.wireOp",EDGE,"E469")}),1.0]])]});
            var Q31;
            Q31=makeQuery(id+"F0.imprint","IMPRINT",FACE,{"disambiguationData":[TD([[makeQuery(id+"F0.imprint","IMPRINT",EDGE,{"derivedFrom":sQuery(id+"F0.wireOp",EDGE,"E177")}),-1.0]])]});
            var Q32;
            Q32=makeQuery(id+"F0.imprint","IMPRINT",FACE,{"disambiguationData":[TD([[makeQuery(id+"F0.imprint","IMPRINT",EDGE,{"derivedFrom":sQuery(id+"F0.wireOp",EDGE,"E331")}),1.0]])]});
            var Q33;
            Q33=makeQuery(id+"F0.imprint","IMPRINT",FACE,{"disambiguationData":[TD([[makeQuery(id+"F0.imprint","IMPRINT",EDGE,{"derivedFrom":sQuery(id+"F0.wireOp",EDGE,"E507")}),1.0]])]});
            var Q34;
            Q34=makeQuery(id+"F0.imprint","IMPRINT",FACE,{"disambiguationData":[TD([[makeQuery(id+"F0.imprint","IMPRINT",EDGE,{"derivedFrom":sQuery(id+"F0.wireOp",EDGE,"E507")}),-1.0]])]});
            var Q35;
            Q35=makeQuery(id+"F0.imprint","IMPRINT",FACE,{"disambiguationData":[TD([[makeQuery(id+"F0.imprint","IMPRINT",EDGE,{"derivedFrom":sQuery(id+"F0.wireOp",EDGE,"E171")}),-1.0]])]});
            var Q36;
            Q36=makeQuery(id+"F0.imprint","IMPRINT",FACE,{"disambiguationData":[TD([[makeQuery(id+"F0.imprint","IMPRINT",EDGE,{"derivedFrom":sQuery(id+"F0.wireOp",EDGE,"E357")}),1.0]])]});
            var Q37;
            Q37=makeQuery(id+"F0.imprint","IMPRINT",FACE,{"disambiguationData":[TD([[makeQuery(id+"F0.imprint","IMPRINT",EDGE,{"derivedFrom":sQuery(id+"F0.wireOp",EDGE,"E158")}),-1.0]])]});
            var Q38;
            Q38=makeQuery(id+"F0.imprint","IMPRINT",FACE,{"disambiguationData":[TD([[makeQuery(id+"F0.imprint","IMPRINT",EDGE,{"derivedFrom":sQuery(id+"F0.wireOp",EDGE,"E421")}),1.0]])]});
            var Q39;
            Q39=makeQuery(id+"F0.imprint","IMPRINT",FACE,{"disambiguationData":[TD([[makeQuery(id+"F0.imprint","IMPRINT",EDGE,{"derivedFrom":sQuery(id+"F0.wireOp",EDGE,"E121")}),1.0]])]});
            var Q40;
            Q40=makeQuery(id+"F0.imprint","IMPRINT",FACE,{"disambiguationData":[TD([[makeQuery(id+"F0.imprint","IMPRINT",EDGE,{"derivedFrom":sQuery(id+"F0.wireOp",EDGE,"E305")}),1.0]])]});
            var Q41;
            Q41=makeQuery(id+"F0.imprint","IMPRINT",FACE,{"disambiguationData":[TD([[makeQuery(id+"F0.imprint","IMPRINT",EDGE,{"derivedFrom":sQuery(id+"F0.wireOp",EDGE,"E239")}),1.0]])]});
            var Q42;
            Q42=makeQuery(id+"F0.imprint","IMPRINT",FACE,{"disambiguationData":[TD([[makeQuery(id+"F0.imprint","IMPRINT",EDGE,{"derivedFrom":sQuery(id+"F0.wireOp",EDGE,"E190")}),1.0]])]});
            var Q43;
            Q43=makeQuery(id+"F0.imprint","IMPRINT",FACE,{"disambiguationData":[TD([[makeQuery(id+"F0.imprint","IMPRINT",EDGE,{"derivedFrom":sQuery(id+"F0.wireOp",EDGE,"E461")}),1.0]])]});
            var Q44;
            Q44=makeQuery(id+"F0.imprint","IMPRINT",FACE,{"disambiguationData":[TD([[makeQuery(id+"F0.imprint","IMPRINT",EDGE,{"derivedFrom":sQuery(id+"F0.wireOp",EDGE,"E112")}),1.0]])]});
            var Q45;
            Q45=makeQuery(id+"F0.imprint","IMPRINT",FACE,{"disambiguationData":[TD([[makeQuery(id+"F0.imprint","IMPRINT",EDGE,{"derivedFrom":sQuery(id+"F0.wireOp",EDGE,"E52")}),1.0]])]});
            var Q46;
            Q46=makeQuery(id+"F0.imprint","IMPRINT",FACE,{"disambiguationData":[TD([[makeQuery(id+"F0.imprint","IMPRINT",EDGE,{"derivedFrom":sQuery(id+"F0.wireOp",EDGE,"E345")}),-1.0]])]});
            var Q47;
            Q47=makeQuery(id+"F0.imprint","IMPRINT",FACE,{"disambiguationData":[TD([[makeQuery(id+"F0.imprint","IMPRINT",EDGE,{"derivedFrom":sQuery(id+"F0.wireOp",EDGE,"E74")}),-1.0]])]});
            var Q48;
            Q48=makeQuery(id+"F0.imprint","IMPRINT",FACE,{"disambiguationData":[TD([[makeQuery(id+"F0.imprint","IMPRINT",EDGE,{"derivedFrom":sQuery(id+"F0.wireOp",EDGE,"E82")}),-1.0]])]});
            extrude(context, id + "F1", {"entities" : qUnion([Q0, Q1, Q2, Q3, Q4, Q5, Q6, Q7, Q8, Q9, Q10, Q11, Q12, Q13, Q14, Q15, Q16, Q17, Q18, Q19, Q20, Q21, Q22, Q23, Q24, Q25, Q26, Q27, Q28, Q29, Q30, Q31, Q32, Q33, Q34, Q35, Q36, Q37, Q38, Q39, Q40, Q41, Q42, Q43, Q44, Q45, Q46, Q47, Q48]), "depth" : 12.7 * mm});
        }
        {
            var Q0;
            Q0=makeQuery(id+"F0.imprint","IMPRINT",FACE,{"disambiguationData":[TD([[makeQuery(id+"F0.imprint","IMPRINT",EDGE,{"derivedFrom":sQuery(id+"F0.wireOp",EDGE,"E1")}),-1.0]])]});
            var Q1;
            Q1=makeQuery(id+"F0.imprint","IMPRINT",FACE,{"disambiguationData":[TD([[makeQuery(id+"F0.imprint","IMPRINT",EDGE,{"derivedFrom":sQuery(id+"F0.wireOp",EDGE,"E542")}),-1.0]])]});
            var Q2;
            Q2=makeQuery(id+"F0.imprint","IMPRINT",FACE,{"disambiguationData":[TD([[makeQuery(id+"F0.imprint","IMPRINT",EDGE,{"derivedFrom":sQuery(id+"F0.wireOp",EDGE,"E121")}),-1.0]])]});
            var Q3;
            Q3=makeQuery(id+"F0.imprint","IMPRINT",FACE,{"disambiguationData":[TD([[makeQuery(id+"F0.imprint","IMPRINT",EDGE,{"derivedFrom":sQuery(id+"F0.wireOp",EDGE,"E592")}),-1.0]])]});
            var Q4;
            {var subQ0=sQuery(id+"F0.wireOp",EDGE,"E583");Q4=makeQuery(id+"F0.imprint","IMPRINT",FACE,{"disambiguationData":[TD([[makeQuery(id+"F0.imprint","IMPRINT",EDGE,{"derivedFrom":subQ0}),1.0]])]});}
            var Q5;
            Q5=makeQuery(id+"F0.imprint","IMPRINT",FACE,{"disambiguationData":[TD([[makeQuery(id+"F0.imprint","IMPRINT",EDGE,{"derivedFrom":sQuery(id+"F0.wireOp",EDGE,"E650")}),-1.0]])]});
            var Q6;
            {var subQ0=sQuery(id+"F0.wireOp",EDGE,"E532");Q6=makeQuery(id+"F0.imprint","IMPRINT",FACE,{"disambiguationData":[TD([[makeQuery(id+"F0.imprint","IMPRINT",EDGE,{"derivedFrom":subQ0}),1.0]])]});}
            var Q7;
            Q7=makeQuery(id+"F0.imprint","IMPRINT",FACE,{"disambiguationData":[TD([[makeQuery(id+"F0.imprint","IMPRINT",EDGE,{"derivedFrom":sQuery(id+"F0.wireOp",EDGE,"E52")}),1.0]])]});
            var Q8;
            Q8=makeQuery(id+"F0.imprint","IMPRINT",FACE,{"disambiguationData":[TD([[makeQuery(id+"F0.imprint","IMPRINT",EDGE,{"derivedFrom":sQuery(id+"F0.wireOp",EDGE,"E90")}),1.0]])]});
            var Q9;
            Q9=makeQuery(id+"F0.imprint","IMPRINT",FACE,{"disambiguationData":[TD([[makeQuery(id+"F0.imprint","IMPRINT",EDGE,{"derivedFrom":sQuery(id+"F0.wireOp",EDGE,"E369")}),1.0]])]});
            var Q10;
            Q10=makeQuery(id+"F0.imprint","IMPRINT",FACE,{"disambiguationData":[TD([[makeQuery(id+"F0.imprint","IMPRINT",EDGE,{"derivedFrom":sQuery(id+"F0.wireOp",EDGE,"E379")}),1.0]])]});
            var Q11;
            Q11=makeQuery(id+"F0.imprint","IMPRINT",FACE,{"disambiguationData":[TD([[makeQuery(id+"F0.imprint","IMPRINT",EDGE,{"derivedFrom":sQuery(id+"F0.wireOp",EDGE,"E383")}),1.0]])]});
            var Q12;
            Q12=makeQuery(id+"F0.imprint","IMPRINT",FACE,{"disambiguationData":[TD([[makeQuery(id+"F0.imprint","IMPRINT",EDGE,{"derivedFrom":sQuery(id+"F0.wireOp",EDGE,"E387")}),1.0]])]});
            var Q13;
            Q13=makeQuery(id+"F0.imprint","IMPRINT",FACE,{"disambiguationData":[TD([[makeQuery(id+"F0.imprint","IMPRINT",EDGE,{"derivedFrom":sQuery(id+"F0.wireOp",EDGE,"E409")}),1.0]])]});
            var Q14;
            Q14=makeQuery(id+"F0.imprint","IMPRINT",FACE,{"disambiguationData":[TD([[makeQuery(id+"F0.imprint","IMPRINT",EDGE,{"derivedFrom":sQuery(id+"F0.wireOp",EDGE,"E421")}),1.0]])]});
            var Q15;
            Q15=makeQuery(id+"F0.imprint","IMPRINT",FACE,{"disambiguationData":[TD([[makeQuery(id+"F0.imprint","IMPRINT",EDGE,{"derivedFrom":sQuery(id+"F0.wireOp",EDGE,"E469")}),1.0]])]});
            var Q16;
            Q16=makeQuery(id+"F0.imprint","IMPRINT",FACE,{"disambiguationData":[TD([[makeQuery(id+"F0.imprint","IMPRINT",EDGE,{"derivedFrom":sQuery(id+"F0.wireOp",EDGE,"E491")}),-1.0]])]});
            var Q17;
            Q17=makeQuery(id+"F0.imprint","IMPRINT",FACE,{"disambiguationData":[TD([[makeQuery(id+"F0.imprint","IMPRINT",EDGE,{"derivedFrom":sQuery(id+"F0.wireOp",EDGE,"E507")}),1.0]])]});
            extrude(context, id + "F2", {"entities" : qUnion([Q0, Q1, Q2, Q3, Q4, Q5, Q6, Q7, Q8, Q9, Q10, Q11, Q12, Q13, Q14, Q15, Q16, Q17]), "operationType" : NewBodyOperationType.ADD, "depth" : 14.48 * mm});
        }
        {
            var Q0;
            Q0=makeQuery(id+"F0.imprint","IMPRINT",FACE,{"disambiguationData":[TD([[makeQuery(id+"F0.imprint","IMPRINT",EDGE,{"derivedFrom":sQuery(id+"F0.wireOp",EDGE,"E120")}),-1.0]])]});
            var Q1;
            Q1=makeQuery(id+"F0.imprint","IMPRINT",FACE,{"disambiguationData":[TD([[makeQuery(id+"F0.imprint","IMPRINT",EDGE,{"derivedFrom":sQuery(id+"F0.wireOp",EDGE,"E629")}),1.0]])]});
            extrude(context, id + "F3", {"entities" : qUnion([Q0, Q1]), "operationType" : NewBodyOperationType.ADD, "depth" : 15.5 * mm});
        }
        {
            var Q0;
            Q0=makeQuery(id+"F0.imprint","IMPRINT",FACE,{"disambiguationData":[TD([[makeQuery(id+"F0.imprint","IMPRINT",EDGE,{"derivedFrom":sQuery(id+"F0.wireOp",EDGE,"E745")}),-1.0]])]});
            var Q1;
            Q1=makeQuery(id+"F0.imprint","IMPRINT",FACE,{"disambiguationData":[TD([[makeQuery(id+"F0.imprint","IMPRINT",EDGE,{"derivedFrom":sQuery(id+"F0.wireOp",EDGE,"E507")}),-1.0]])]});
            extrude(context, id + "F4", {"entities" : qUnion([Q0, Q1]), "operationType" : NewBodyOperationType.ADD, "depth" : 14.33 * mm});
        }
        {
            var Q0;
            Q0=makeQuery(id+"F0.imprint","IMPRINT",FACE,{"disambiguationData":[TD([[makeQuery(id+"F0.imprint","IMPRINT",EDGE,{"derivedFrom":sQuery(id+"F0.wireOp",EDGE,"E714")}),1.0]])]});
            var Q1;
            Q1=makeQuery(id+"F0.imprint","IMPRINT",FACE,{"disambiguationData":[TD([[makeQuery(id+"F0.imprint","IMPRINT",EDGE,{"derivedFrom":sQuery(id+"F0.wireOp",EDGE,"E120")}),1.0]])]});
            var Q2;
            Q2=makeQuery(id+"F0.imprint","IMPRINT",FACE,{"disambiguationData":[TD([[makeQuery(id+"F0.imprint","IMPRINT",EDGE,{"derivedFrom":sQuery(id+"F0.wireOp",EDGE,"E700")}),1.0]])]});
            var Q3;
            Q3=makeQuery(id+"F0.imprint","IMPRINT",FACE,{"disambiguationData":[TD([[makeQuery(id+"F0.imprint","IMPRINT",EDGE,{"derivedFrom":sQuery(id+"F0.wireOp",EDGE,"E721")}),-1.0]])]});
            var Q4;
            Q4=makeQuery(id+"F0.imprint","IMPRINT",FACE,{"disambiguationData":[TD([[makeQuery(id+"F0.imprint","IMPRINT",EDGE,{"derivedFrom":sQuery(id+"F0.wireOp",EDGE,"E707")}),-1.0]])]});
            var Q5;
            Q5=makeQuery(id+"F0.imprint","IMPRINT",FACE,{"disambiguationData":[TD([[makeQuery(id+"F0.imprint","IMPRINT",EDGE,{"derivedFrom":sQuery(id+"F0.wireOp",EDGE,"E629")}),-1.0]])]});
            var Q6;
            Q6=makeQuery(id+"F0.imprint","IMPRINT",FACE,{"disambiguationData":[TD([[makeQuery(id+"F0.imprint","IMPRINT",EDGE,{"derivedFrom":sQuery(id+"F0.wireOp",EDGE,"E728")}),-1.0]])]});
            var Q7;
            Q7=makeQuery(id+"F0.imprint","IMPRINT",FACE,{"disambiguationData":[TD([[makeQuery(id+"F0.imprint","IMPRINT",EDGE,{"derivedFrom":sQuery(id+"F0.wireOp",EDGE,"E50")}),1.0]])]});
            var Q8;
            Q8=makeQuery(id+"F0.imprint","IMPRINT",FACE,{"disambiguationData":[TD([[makeQuery(id+"F0.imprint","IMPRINT",EDGE,{"derivedFrom":sQuery(id+"F0.wireOp",EDGE,"E51")}),1.0]])]});
            var Q9;
            Q9=makeQuery(id+"F0.imprint","IMPRINT",FACE,{"disambiguationData":[TD([[makeQuery(id+"F0.imprint","IMPRINT",EDGE,{"derivedFrom":sQuery(id+"F0.wireOp",EDGE,"E121")}),1.0]])]});
            var Q10;
            Q10=makeQuery(id+"F0.imprint","IMPRINT",FACE,{"disambiguationData":[TD([[makeQuery(id+"F0.imprint","IMPRINT",EDGE,{"derivedFrom":sQuery(id+"F0.wireOp",EDGE,"E158")}),-1.0]])]});
            var Q11;
            Q11=makeQuery(id+"F0.imprint","IMPRINT",FACE,{"disambiguationData":[TD([[makeQuery(id+"F0.imprint","IMPRINT",EDGE,{"derivedFrom":sQuery(id+"F0.wireOp",EDGE,"E171")}),-1.0]])]});
            var Q12;
            Q12=makeQuery(id+"F0.imprint","IMPRINT",FACE,{"disambiguationData":[TD([[makeQuery(id+"F0.imprint","IMPRINT",EDGE,{"derivedFrom":sQuery(id+"F0.wireOp",EDGE,"E177")}),-1.0]])]});
            var Q13;
            Q13=makeQuery(id+"F0.imprint","IMPRINT",FACE,{"disambiguationData":[TD([[makeQuery(id+"F0.imprint","IMPRINT",EDGE,{"derivedFrom":sQuery(id+"F0.wireOp",EDGE,"E190")}),1.0]])]});
            var Q14;
            Q14=makeQuery(id+"F0.imprint","IMPRINT",FACE,{"disambiguationData":[TD([[makeQuery(id+"F0.imprint","IMPRINT",EDGE,{"derivedFrom":sQuery(id+"F0.wireOp",EDGE,"E231")}),1.0]])]});
            var Q15;
            Q15=makeQuery(id+"F0.imprint","IMPRINT",FACE,{"disambiguationData":[TD([[makeQuery(id+"F0.imprint","IMPRINT",EDGE,{"derivedFrom":sQuery(id+"F0.wireOp",EDGE,"E239")}),1.0]])]});
            var Q16;
            Q16=makeQuery(id+"F0.imprint","IMPRINT",FACE,{"disambiguationData":[TD([[makeQuery(id+"F0.imprint","IMPRINT",EDGE,{"derivedFrom":sQuery(id+"F0.wireOp",EDGE,"E297")}),1.0]])]});
            var Q17;
            Q17=makeQuery(id+"F0.imprint","IMPRINT",FACE,{"disambiguationData":[TD([[makeQuery(id+"F0.imprint","IMPRINT",EDGE,{"derivedFrom":sQuery(id+"F0.wireOp",EDGE,"E305")}),1.0]])]});
            var Q18;
            Q18=makeQuery(id+"F0.imprint","IMPRINT",FACE,{"disambiguationData":[TD([[makeQuery(id+"F0.imprint","IMPRINT",EDGE,{"derivedFrom":sQuery(id+"F0.wireOp",EDGE,"E331")}),1.0]])]});
            var Q19;
            Q19=makeQuery(id+"F0.imprint","IMPRINT",FACE,{"disambiguationData":[TD([[makeQuery(id+"F0.imprint","IMPRINT",EDGE,{"derivedFrom":sQuery(id+"F0.wireOp",EDGE,"E361")}),1.0]])]});
            extrude(context, id + "F5", {"entities" : qUnion([Q0, Q1, Q2, Q3, Q4, Q5, Q6, Q7, Q8, Q9, Q10, Q11, Q12, Q13, Q14, Q15, Q16, Q17, Q18, Q19]), "operationType" : NewBodyOperationType.ADD, "depth" : 16.43 * mm});
        }
        {
            var Q0;
            Q0=makeQuery(id+"F0.imprint","IMPRINT",FACE,{"disambiguationData":[TD([[makeQuery(id+"F0.imprint","IMPRINT",EDGE,{"derivedFrom":sQuery(id+"F0.wireOp",EDGE,"E357")}),1.0]])]});
            var Q1;
            Q1=makeQuery(id+"F0.imprint","IMPRINT",FACE,{"disambiguationData":[TD([[makeQuery(id+"F0.imprint","IMPRINT",EDGE,{"derivedFrom":sQuery(id+"F0.wireOp",EDGE,"E345")}),-1.0]])]});
            extrude(context, id + "F6", {"entities" : qUnion([Q0, Q1]), "operationType" : NewBodyOperationType.ADD, "depth" : 16.26 * mm});
        }
    });
